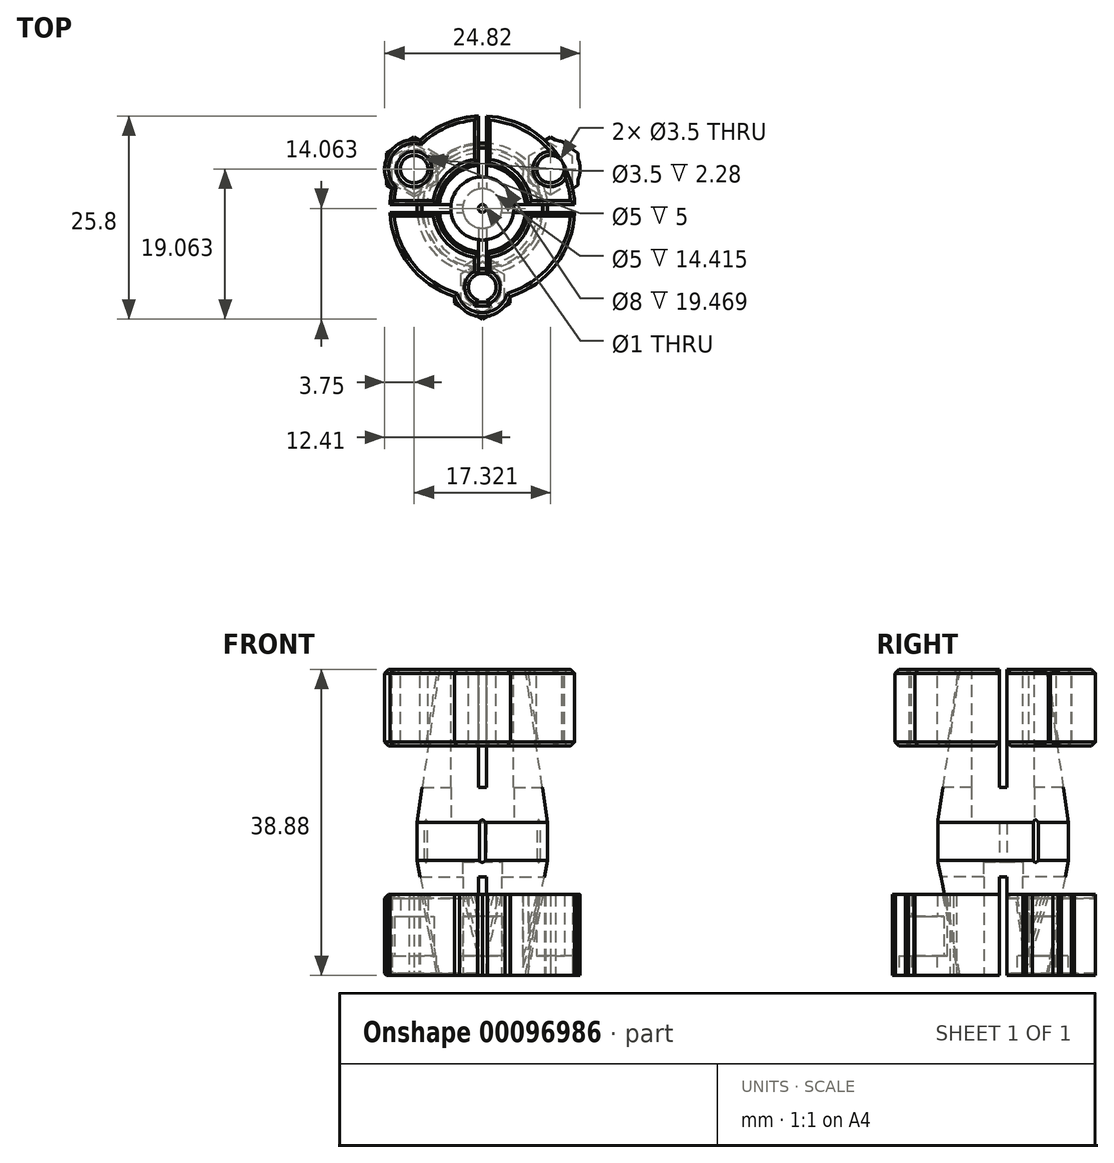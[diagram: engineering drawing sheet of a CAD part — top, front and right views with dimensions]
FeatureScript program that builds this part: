
annotation { "Feature Type Name" : "Feature", "Feature Type Description" : "" }
export const myFeature = defineFeature(function(context is Context, id is Id, definition is map)
    precondition{}
    {
        {
            var Q0;
            Q0=qCreatedBy(makeId("Right.planeOp"),FACE);
            var sketch = newSketch(context, id + "F0", { "sketchPlane" : qUnion([Q0])});
            skLineSegment(sketch, "E0", {"start": v(7.15, -27.2) * mm, "end": v(7.15, -12.78) * mm});
            skLineSegment(sketch, "E1", {"start": v(7.15, -12.78) * mm, "end": v(5.15, -12.78) * mm});
            skLineSegment(sketch, "E2", {"start": v(5.15, -12.78) * mm, "end": v(5.15, -7.78) * mm});
            skLineSegment(sketch, "E3", {"start": v(5.15, -7.78) * mm, "end": v(8.65, -7.78) * mm});
            skLineSegment(sketch, "E4", {"start": v(8.65, -7.78) * mm, "end": v(8.65, 11.68) * mm});
            skLineSegment(sketch, "E5", {"start": v(8.65, 11.68) * mm, "end": v(10.13, 11.68) * mm});
            skLineSegment(sketch, "E6", {"start": v(10.13, 11.68) * mm, "end": v(12.95, -7.78) * mm});
            skLineSegment(sketch, "E7", {"start": v(12.95, -7.78) * mm, "end": v(12.95, -12.57) * mm});
            skLineSegment(sketch, "E8", {"start": v(12.95, -12.57) * mm, "end": v(10.13, -27.2) * mm});
            skLineSegment(sketch, "E9", {"start": v(10.13, -27.2) * mm, "end": v(7.15, -27.2) * mm});
            skLineSegment(sketch, "E10", {"start": v(4.65, -27.22) * mm, "end": v(4.65, -0.97) * mm});
            skLineSegment(sketch, "E11", {"start": v(11.8, 1.95) * mm, "end": v(10.39, 11.68) * mm});
            skPoint(sketch, "E11.startSnap0", {"position": v(11.54, 1.95) * mm});
            skLineSegment(sketch, "E12", {"start": v(10.39, 11.68) * mm, "end": v(16.4, 11.68) * mm});
            skLineSegment(sketch, "E13", {"start": v(16.4, 11.68) * mm, "end": v(16.4, 1.95) * mm});
            skLineSegment(sketch, "E14", {"start": v(16.4, 1.95) * mm, "end": v(11.8, 1.95) * mm});
            skLineSegment(sketch, "E15", {"start": v(10.39, -27.2) * mm, "end": v(12.37, -16.92) * mm});
            skLineSegment(sketch, "E16", {"start": v(12.37, -16.92) * mm, "end": v(16.4, -16.92) * mm});
            skLineSegment(sketch, "E17", {"start": v(16.4, -16.92) * mm, "end": v(16.4, -27.2) * mm});
            skLineSegment(sketch, "E18", {"start": v(16.4, -27.2) * mm, "end": v(10.39, -27.2) * mm});
            skSolve(sketch);
        }
        {
            var Q0;
            Q0=makeQuery(id+"F0.imprint","IMPRINT",FACE,{"disambiguationData":[TD([[makeQuery(id+"F0.imprint","IMPRINT",EDGE,{"derivedFrom":sQuery(id+"F0.wireOp",EDGE,"E0")}),-1.0]])]});
            var Q1;
            Q1=sQuery(id+"F0.wireOp",EDGE,"E10");
            revolve(context, id + "F1", {"entities" : qUnion([Q0]), "axis" : qUnion([Q1]), "revolveType" : RevolveType.FULL});
        }
        {
            var Q0;
            Q0=makeQuery(id+"F0.imprint","IMPRINT",FACE,{"disambiguationData":[TD([[makeQuery(id+"F0.imprint","IMPRINT",EDGE,{"derivedFrom":sQuery(id+"F0.wireOp",EDGE,"E11")}),-1.0]])]});
            var Q1;
            Q1=makeQuery(id+"F0.imprint","IMPRINT",FACE,{"disambiguationData":[TD([[makeQuery(id+"F0.imprint","IMPRINT",EDGE,{"derivedFrom":sQuery(id+"F0.wireOp",EDGE,"E15")}),-1.0]])]});
            var Q2;
            Q2=sQuery(id+"F0.wireOp",EDGE,"E10");
            revolve(context, id + "F2", {"entities" : qUnion([Q0, Q1]), "axis" : qUnion([Q2]), "revolveType" : RevolveType.FULL});
        }
        {
            var Q0;
            Q0=makeQuery(id+"F2.opRevolve","SWEPT_FACE",FACE,{"disambiguationData":[OSD([sQuery(id+"F0.wireOp",EDGE,"E12")])]});
            var sketch = newSketch(context, id + "F3", { "sketchPlane" : qUnion([Q0])});
            skCircle(sketch, "E19", {"center": v(0, 4.65) * mm, "radius": 10 * mm});
            skCircle(sketch, "E20", {"center": v(0, -5.35) * mm, "radius": 1.75 * mm});
            skCircle(sketch, "E21", {"center": v(0, -5.35) * mm, "radius": 3.75 * mm});
            skCircle(sketch, "E22.1.0", {"center": v(8.66, 9.65) * mm, "radius": 1.75 * mm});
            skCircle(sketch, "E22.1.1", {"center": v(8.66, 9.65) * mm, "radius": 3.75 * mm});
            skCircle(sketch, "E22.2.0", {"center": v(-8.66, 9.65) * mm, "radius": 1.75 * mm});
            skCircle(sketch, "E22.2.1", {"center": v(-8.66, 9.65) * mm, "radius": 3.75 * mm});
            skSolve(sketch);
        }
        {
            var Q0;
            {var subQ0=sQuery(id+"F3.wireOp",EDGE,"E20");var subQ1=makeQuery(id+"F2.opRevolve","SWEPT_EDGE",EDGE,{"disambiguationData":[OSD([sQuery(id+"F0.wireOp",EDGE,"E12"),sQuery(id+"F0.wireOp",EDGE,"E13")])]});var subQ2=makeQuery(id+"F3.imprint","INTERSECT",VERTEX,{"disambiguationData":[OD(0.0)],"derivedFrom":[subQ1,subQ0]});Q0=makeQuery(id+"F3.imprint","IMPRINT",FACE,{"disambiguationData":[TD([[makeQuery(id+"F3.imprint","IMPRINT",EDGE,{"disambiguationData":[TD([[subQ2,-1.0]])],"derivedFrom":subQ0}),-1.0]])]});}
            var Q1;
            {var subQ0=sQuery(id+"F3.wireOp",EDGE,"E22.2.0");var subQ1=makeQuery(id+"F2.opRevolve","SWEPT_EDGE",EDGE,{"disambiguationData":[OSD([sQuery(id+"F0.wireOp",EDGE,"E12"),sQuery(id+"F0.wireOp",EDGE,"E13")])]});var subQ2=makeQuery(id+"F3.imprint","INTERSECT",VERTEX,{"disambiguationData":[OD(0.0)],"derivedFrom":[subQ1,subQ0]});Q1=makeQuery(id+"F3.imprint","IMPRINT",FACE,{"disambiguationData":[TD([[makeQuery(id+"F3.imprint","IMPRINT",EDGE,{"disambiguationData":[TD([[subQ2,-1.0]])],"derivedFrom":subQ0}),-1.0]])]});}
            var Q2;
            {var subQ0=sQuery(id+"F3.wireOp",EDGE,"E22.1.0");var subQ1=makeQuery(id+"F2.opRevolve","SWEPT_EDGE",EDGE,{"disambiguationData":[OSD([sQuery(id+"F0.wireOp",EDGE,"E12"),sQuery(id+"F0.wireOp",EDGE,"E13")])]});var subQ2=makeQuery(id+"F3.imprint","INTERSECT",VERTEX,{"disambiguationData":[OD(0.0)],"derivedFrom":[subQ1,subQ0]});Q2=makeQuery(id+"F3.imprint","IMPRINT",FACE,{"disambiguationData":[TD([[makeQuery(id+"F3.imprint","IMPRINT",EDGE,{"disambiguationData":[TD([[subQ2,-1.0]])],"derivedFrom":subQ0}),-1.0]])]});}
            var Q3;
            Q3=makeQuery(id+"F2.opRevolve","SWEPT_FACE",FACE,{"disambiguationData":[OSD([sQuery(id+"F0.wireOp",EDGE,"E14")])]});
            extrude(context, id + "F4", {"entities" : qUnion([Q0, Q1, Q2]), "operationType" : NewBodyOperationType.ADD, "endBound" : BoundingType.UP_TO_SURFACE, "oppositeDirection" : true, "endBoundEntityFace" : qUnion([Q3]), "depth" : 25 * mm});
        }
        {
            var Q0;
            {var subQ0=sQuery(id+"F3.wireOp",EDGE,"E20");var subQ1=sQuery(id+"F3.wireOp",EDGE,"E19");var subQ2=makeQuery(id+"F3.imprint","INTERSECT",VERTEX,{"disambiguationData":[OD(0.0)],"derivedFrom":[subQ1,subQ0]});Q0=makeQuery(id+"F3.imprint","IMPRINT",FACE,{"disambiguationData":[TD([[makeQuery(id+"F3.imprint","IMPRINT",EDGE,{"disambiguationData":[TD([[subQ2,-1.0]])],"derivedFrom":subQ1}),-1.0]])]});}
            var Q1;
            {var subQ0=sQuery(id+"F3.wireOp",EDGE,"E20");var subQ1=sQuery(id+"F3.wireOp",EDGE,"E19");var subQ2=makeQuery(id+"F3.imprint","INTERSECT",VERTEX,{"disambiguationData":[OD(0.0)],"derivedFrom":[subQ1,subQ0]});Q1=makeQuery(id+"F3.imprint","IMPRINT",FACE,{"disambiguationData":[TD([[makeQuery(id+"F3.imprint","IMPRINT",EDGE,{"disambiguationData":[TD([[subQ2,-1.0]])],"derivedFrom":subQ1}),1.0]])]});}
            var Q2;
            {var subQ0=sQuery(id+"F3.wireOp",EDGE,"E22.1.0");var subQ1=sQuery(id+"F3.wireOp",EDGE,"E19");var subQ2=makeQuery(id+"F3.imprint","INTERSECT",VERTEX,{"disambiguationData":[OD(0.0)],"derivedFrom":[subQ1,subQ0]});Q2=makeQuery(id+"F3.imprint","IMPRINT",FACE,{"disambiguationData":[TD([[makeQuery(id+"F3.imprint","IMPRINT",EDGE,{"disambiguationData":[TD([[subQ2,-1.0]])],"derivedFrom":subQ1}),1.0]])]});}
            var Q3;
            {var subQ0=sQuery(id+"F3.wireOp",EDGE,"E22.1.0");var subQ1=sQuery(id+"F3.wireOp",EDGE,"E19");var subQ2=makeQuery(id+"F3.imprint","INTERSECT",VERTEX,{"disambiguationData":[OD(0.0)],"derivedFrom":[subQ1,subQ0]});Q3=makeQuery(id+"F3.imprint","IMPRINT",FACE,{"disambiguationData":[TD([[makeQuery(id+"F3.imprint","IMPRINT",EDGE,{"disambiguationData":[TD([[subQ2,-1.0]])],"derivedFrom":subQ1}),-1.0]])]});}
            var Q4;
            {var subQ0=sQuery(id+"F3.wireOp",EDGE,"E22.2.0");var subQ1=sQuery(id+"F3.wireOp",EDGE,"E19");var subQ2=makeQuery(id+"F3.imprint","INTERSECT",VERTEX,{"disambiguationData":[OD(0.0)],"derivedFrom":[subQ1,subQ0]});Q4=makeQuery(id+"F3.imprint","IMPRINT",FACE,{"disambiguationData":[TD([[makeQuery(id+"F3.imprint","IMPRINT",EDGE,{"disambiguationData":[TD([[subQ2,-1.0]])],"derivedFrom":subQ1}),1.0]])]});}
            var Q5;
            {var subQ0=sQuery(id+"F3.wireOp",EDGE,"E22.2.0");var subQ1=sQuery(id+"F3.wireOp",EDGE,"E19");var subQ2=makeQuery(id+"F3.imprint","INTERSECT",VERTEX,{"disambiguationData":[OD(0.0)],"derivedFrom":[subQ1,subQ0]});Q5=makeQuery(id+"F3.imprint","IMPRINT",FACE,{"disambiguationData":[TD([[makeQuery(id+"F3.imprint","IMPRINT",EDGE,{"disambiguationData":[TD([[subQ2,-1.0]])],"derivedFrom":subQ1}),-1.0]])]});}
            extrude(context, id + "F5", {"entities" : qUnion([Q0, Q1, Q2, Q3, Q4, Q5]), "operationType" : NewBodyOperationType.REMOVE, "oppositeDirection" : true, "depth" : 25 * mm});
        }
        {
            var Q0;
            Q0=makeQuery(id+"F2.opRevolve","SWEPT_FACE",FACE,{"disambiguationData":[OSD([sQuery(id+"F0.wireOp",EDGE,"E18")])]});
            var sketch = newSketch(context, id + "F6", { "sketchPlane" : qUnion([Q0])});
            skArc(sketch, "E23.0.0", {"start": v(-3.55, 6.54) * mm, "mid": v(-10.17, 1.22) * mm, "end": v(-11.47, -7.17) * mm});
            skArc(sketch, "E23.0.1", {"start": v(-11.47, -7.17) * mm, "mid": v(-11.9, -11.53) * mm, "end": v(-7.92, -13.33) * mm});
            skArc(sketch, "E23.0.2", {"start": v(-7.92, -13.33) * mm, "mid": v(0, -16.4) * mm, "end": v(7.92, -13.33) * mm});
            skArc(sketch, "E23.0.3", {"start": v(7.92, -13.33) * mm, "mid": v(11.9, -11.53) * mm, "end": v(11.47, -7.17) * mm});
            skArc(sketch, "E23.0.4", {"start": v(11.47, -7.17) * mm, "mid": v(10.17, 1.22) * mm, "end": v(3.55, 6.54) * mm});
            skArc(sketch, "E23.0.5", {"start": v(3.55, 6.54) * mm, "mid": v(0, 9.1) * mm, "end": v(-3.55, 6.54) * mm});
            skCircle(sketch, "E24", {"center": v(8.66, -9.65) * mm, "radius": 1.75 * mm});
            skCircle(sketch, "E25", {"center": v(-8.66, -9.65) * mm, "radius": 1.75 * mm});
            skCircle(sketch, "E26", {"center": v(0, 5.35) * mm, "radius": 1.75 * mm});
            skSolve(sketch);
        }
        {
            var Q0;
            {var subQ0=sQuery(id+"F6.wireOp",EDGE,"E23.0.5");Q0=makeQuery(id+"F6.imprint","IMPRINT",FACE,{"disambiguationData":[TD([[makeQuery(id+"F6.imprint","IMPRINT",EDGE,{"derivedFrom":subQ0}),1.0]])]});}
            var Q1;
            {var subQ0=sQuery(id+"F6.wireOp",EDGE,"E23.0.3");Q1=makeQuery(id+"F6.imprint","IMPRINT",FACE,{"disambiguationData":[TD([[makeQuery(id+"F6.imprint","IMPRINT",EDGE,{"derivedFrom":subQ0}),1.0]])]});}
            var Q2;
            {var subQ0=sQuery(id+"F6.wireOp",EDGE,"E23.0.1");Q2=makeQuery(id+"F6.imprint","IMPRINT",FACE,{"disambiguationData":[TD([[makeQuery(id+"F6.imprint","IMPRINT",EDGE,{"derivedFrom":subQ0}),1.0]])]});}
            var Q3;
            Q3=makeQuery(id+"F2.opRevolve","SWEPT_FACE",FACE,{"disambiguationData":[OSD([sQuery(id+"F0.wireOp",EDGE,"E16")])]});
            extrude(context, id + "F7", {"entities" : qUnion([Q0, Q1, Q2]), "operationType" : NewBodyOperationType.ADD, "endBound" : BoundingType.UP_TO_SURFACE, "oppositeDirection" : true, "endBoundEntityFace" : qUnion([Q3]), "depth" : 25 * mm});
        }
        {
            var Q0;
            {var subQ0=sQuery(id+"F6.wireOp",EDGE,"E26");var subQ1=makeQuery(id+"F2.opRevolve","SWEPT_EDGE",EDGE,{"disambiguationData":[OSD([sQuery(id+"F0.wireOp",EDGE,"E17"),sQuery(id+"F0.wireOp",EDGE,"E18")])]});var subQ2=makeQuery(id+"F6.imprint","INTERSECT",VERTEX,{"disambiguationData":[OD(0.0)],"derivedFrom":[subQ1,subQ0]});Q0=makeQuery(id+"F6.imprint","IMPRINT",FACE,{"disambiguationData":[TD([[makeQuery(id+"F6.imprint","IMPRINT",EDGE,{"disambiguationData":[TD([[subQ2,-1.0]])],"derivedFrom":subQ0}),1.0]])]});}
            var Q1;
            {var subQ0=sQuery(id+"F6.wireOp",EDGE,"E25");var subQ1=makeQuery(id+"F2.opRevolve","SWEPT_EDGE",EDGE,{"disambiguationData":[OSD([sQuery(id+"F0.wireOp",EDGE,"E17"),sQuery(id+"F0.wireOp",EDGE,"E18")])]});var subQ2=makeQuery(id+"F6.imprint","INTERSECT",VERTEX,{"disambiguationData":[OD(0.0)],"derivedFrom":[subQ1,subQ0]});Q1=makeQuery(id+"F6.imprint","IMPRINT",FACE,{"disambiguationData":[TD([[makeQuery(id+"F6.imprint","IMPRINT",EDGE,{"disambiguationData":[TD([[subQ2,1.0]])],"derivedFrom":subQ0}),1.0]])]});}
            var Q2;
            {var subQ0=sQuery(id+"F6.wireOp",EDGE,"E24");var subQ1=makeQuery(id+"F2.opRevolve","SWEPT_EDGE",EDGE,{"disambiguationData":[OSD([sQuery(id+"F0.wireOp",EDGE,"E17"),sQuery(id+"F0.wireOp",EDGE,"E18")])]});var subQ2=makeQuery(id+"F6.imprint","INTERSECT",VERTEX,{"disambiguationData":[OD(0.0)],"derivedFrom":[subQ1,subQ0]});Q2=makeQuery(id+"F6.imprint","IMPRINT",FACE,{"disambiguationData":[TD([[makeQuery(id+"F6.imprint","IMPRINT",EDGE,{"disambiguationData":[TD([[subQ2,1.0]])],"derivedFrom":subQ0}),1.0]])]});}
            extrude(context, id + "F8", {"entities" : qUnion([Q0, Q1, Q2]), "operationType" : NewBodyOperationType.REMOVE, "oppositeDirection" : true, "depth" : 25 * mm});
        }
        {
            var Q0;
            Q0=makeQuery(id+"F1.opRevolve","SWEPT_FACE",FACE,{"disambiguationData":[OSD([sQuery(id+"F0.wireOp",EDGE,"E5")])]});
            var sketch = newSketch(context, id + "F9", { "sketchPlane" : qUnion([Q0])});
            skLineSegment(sketch, "E27.bottom", {"start": v(0.5, 16.55) * mm, "end": v(-0.5, 16.55) * mm});
            skLineSegment(sketch, "E27.top", {"start": v(0.5, -7.24) * mm, "end": v(-0.5, -7.24) * mm});
            skLineSegment(sketch, "E27.left", {"start": v(0.5, 16.55) * mm, "end": v(0.5, -7.24) * mm});
            skLineSegment(sketch, "E27.right", {"start": v(-0.5, 16.55) * mm, "end": v(-0.5, -7.24) * mm});
            skLineSegment(sketch, "E28.bottom", {"start": v(-15.2, 5.15) * mm, "end": v(15.2, 5.15) * mm});
            skLineSegment(sketch, "E28.top", {"start": v(-15.2, 4.15) * mm, "end": v(15.2, 4.15) * mm});
            skLineSegment(sketch, "E28.left", {"start": v(-15.2, 5.15) * mm, "end": v(-15.2, 4.15) * mm});
            skLineSegment(sketch, "E28.right", {"start": v(15.2, 5.15) * mm, "end": v(15.2, 4.15) * mm});
            skPoint(sketch, "E28.middle", {"position": v(0, 4.65) * mm});
            skSolve(sketch);
        }
        {
            var Q0;
            {var subQ0=sQuery(id+"F9.wireOp",EDGE,"E28.bottom");var subQ1=sQuery(id+"F9.wireOp",EDGE,"E27.left");var subQ2=makeQuery(id+"F9.imprint","INTERSECT",VERTEX,{"derivedFrom":[subQ1,subQ0]});Q0=makeQuery(id+"F9.imprint","IMPRINT",FACE,{"disambiguationData":[TD([[makeQuery(id+"F9.imprint","IMPRINT",EDGE,{"disambiguationData":[TD([[subQ2,-1.0]])],"derivedFrom":subQ1}),-1.0]])]});}
            var Q1;
            {var subQ0=sQuery(id+"F9.wireOp",EDGE,"E27.bottom");Q1=makeQuery(id+"F9.imprint","IMPRINT",FACE,{"disambiguationData":[TD([[makeQuery(id+"F9.imprint","IMPRINT",EDGE,{"derivedFrom":subQ0}),1.0]])]});}
            var Q2;
            {var subQ0=sQuery(id+"F9.wireOp",EDGE,"E27.top");Q2=makeQuery(id+"F9.imprint","IMPRINT",FACE,{"disambiguationData":[TD([[makeQuery(id+"F9.imprint","IMPRINT",EDGE,{"derivedFrom":subQ0}),-1.0]])]});}
            var Q3;
            {var subQ0=sQuery(id+"F9.wireOp",EDGE,"E28.bottom");var subQ1=sQuery(id+"F9.wireOp",EDGE,"E27.left");var subQ2=makeQuery(id+"F9.imprint","INTERSECT",VERTEX,{"derivedFrom":[subQ1,subQ0]});Q3=makeQuery(id+"F9.imprint","IMPRINT",FACE,{"disambiguationData":[TD([[makeQuery(id+"F9.imprint","IMPRINT",EDGE,{"disambiguationData":[TD([[subQ2,1.0]])],"derivedFrom":subQ0}),1.0]])]});}
            var Q4;
            {var subQ0=sQuery(id+"F9.wireOp",EDGE,"E28.top");var subQ1=sQuery(id+"F9.wireOp",EDGE,"E27.left");var subQ2=makeQuery(id+"F9.imprint","INTERSECT",VERTEX,{"derivedFrom":[subQ1,subQ0]});Q4=makeQuery(id+"F9.imprint","IMPRINT",FACE,{"disambiguationData":[TD([[makeQuery(id+"F9.imprint","IMPRINT",EDGE,{"disambiguationData":[TD([[subQ2,1.0]])],"derivedFrom":subQ0}),-1.0]])]});}
            var Q5;
            {var subQ0=sQuery(id+"F9.wireOp",EDGE,"E27.left");var subQ1=sQuery(id+"F0.wireOp",EDGE,"E5");var subQ2=makeQuery(id+"F1.opRevolve","SWEPT_EDGE",EDGE,{"disambiguationData":[OSD([subQ1,sQuery(id+"F0.wireOp",EDGE,"E6")])]});var subQ3=makeQuery(id+"F9.imprint","INTERSECT",VERTEX,{"disambiguationData":[OD(0.0)],"derivedFrom":[subQ2,subQ0]});Q5=makeQuery(id+"F9.imprint","IMPRINT",FACE,{"disambiguationData":[TD([[makeQuery(id+"F9.imprint","IMPRINT",EDGE,{"disambiguationData":[TD([[subQ3,-1.0]])],"derivedFrom":subQ0}),-1.0]])]});}
            var Q6;
            {var subQ0=sQuery(id+"F9.wireOp",EDGE,"E28.bottom");var subQ1=sQuery(id+"F9.wireOp",EDGE,"E27.left");var subQ2=makeQuery(id+"F9.imprint","INTERSECT",VERTEX,{"derivedFrom":[subQ1,subQ0]});Q6=makeQuery(id+"F9.imprint","IMPRINT",FACE,{"disambiguationData":[TD([[makeQuery(id+"F9.imprint","IMPRINT",EDGE,{"disambiguationData":[TD([[subQ2,-1.0]])],"derivedFrom":subQ1}),-1.0]])]});}
            var Q7;
            {var subQ0=sQuery(id+"F9.wireOp",EDGE,"E27.bottom");Q7=makeQuery(id+"F9.imprint","IMPRINT",FACE,{"disambiguationData":[TD([[makeQuery(id+"F9.imprint","IMPRINT",EDGE,{"derivedFrom":subQ0}),1.0]])]});}
            var Q8;
            {var subQ0=sQuery(id+"F9.wireOp",EDGE,"E27.top");Q8=makeQuery(id+"F9.imprint","IMPRINT",FACE,{"disambiguationData":[TD([[makeQuery(id+"F9.imprint","IMPRINT",EDGE,{"derivedFrom":subQ0}),-1.0]])]});}
            var Q9;
            {var subQ0=sQuery(id+"F9.wireOp",EDGE,"E28.bottom");var subQ1=sQuery(id+"F9.wireOp",EDGE,"E27.left");var subQ2=makeQuery(id+"F9.imprint","INTERSECT",VERTEX,{"derivedFrom":[subQ1,subQ0]});Q9=makeQuery(id+"F9.imprint","IMPRINT",FACE,{"disambiguationData":[TD([[makeQuery(id+"F9.imprint","IMPRINT",EDGE,{"disambiguationData":[TD([[subQ2,1.0]])],"derivedFrom":subQ0}),1.0]])]});}
            var Q10;
            {var subQ0=sQuery(id+"F9.wireOp",EDGE,"E28.top");var subQ1=sQuery(id+"F9.wireOp",EDGE,"E27.left");var subQ2=makeQuery(id+"F9.imprint","INTERSECT",VERTEX,{"derivedFrom":[subQ1,subQ0]});Q10=makeQuery(id+"F9.imprint","IMPRINT",FACE,{"disambiguationData":[TD([[makeQuery(id+"F9.imprint","IMPRINT",EDGE,{"disambiguationData":[TD([[subQ2,1.0]])],"derivedFrom":subQ0}),-1.0]])]});}
            var Q11;
            {var subQ0=sQuery(id+"F9.wireOp",EDGE,"E27.left");var subQ1=sQuery(id+"F0.wireOp",EDGE,"E5");var subQ2=makeQuery(id+"F1.opRevolve","SWEPT_EDGE",EDGE,{"disambiguationData":[OSD([subQ1,sQuery(id+"F0.wireOp",EDGE,"E6")])]});var subQ3=makeQuery(id+"F9.imprint","INTERSECT",VERTEX,{"disambiguationData":[OD(0.0)],"derivedFrom":[subQ2,subQ0]});Q11=makeQuery(id+"F9.imprint","IMPRINT",FACE,{"disambiguationData":[TD([[makeQuery(id+"F9.imprint","IMPRINT",EDGE,{"disambiguationData":[TD([[subQ3,-1.0]])],"derivedFrom":subQ0}),-1.0]])]});}
            var Q12;
            {var subQ0=sQuery(id+"F9.wireOp",EDGE,"E28.bottom");var subQ1=sQuery(id+"F9.wireOp",EDGE,"E27.left");var subQ2=makeQuery(id+"F9.imprint","INTERSECT",VERTEX,{"derivedFrom":[subQ1,subQ0]});Q12=makeQuery(id+"F9.imprint","IMPRINT",FACE,{"disambiguationData":[TD([[makeQuery(id+"F9.imprint","IMPRINT",EDGE,{"disambiguationData":[TD([[subQ2,-1.0]])],"derivedFrom":subQ1}),-1.0]])]});}
            var Q13;
            {var subQ0=sQuery(id+"F9.wireOp",EDGE,"E27.bottom");Q13=makeQuery(id+"F9.imprint","IMPRINT",FACE,{"disambiguationData":[TD([[makeQuery(id+"F9.imprint","IMPRINT",EDGE,{"derivedFrom":subQ0}),1.0]])]});}
            var Q14;
            {var subQ0=sQuery(id+"F9.wireOp",EDGE,"E27.top");Q14=makeQuery(id+"F9.imprint","IMPRINT",FACE,{"disambiguationData":[TD([[makeQuery(id+"F9.imprint","IMPRINT",EDGE,{"derivedFrom":subQ0}),-1.0]])]});}
            var Q15;
            {var subQ0=sQuery(id+"F9.wireOp",EDGE,"E28.bottom");var subQ1=sQuery(id+"F9.wireOp",EDGE,"E27.left");var subQ2=makeQuery(id+"F9.imprint","INTERSECT",VERTEX,{"derivedFrom":[subQ1,subQ0]});Q15=makeQuery(id+"F9.imprint","IMPRINT",FACE,{"disambiguationData":[TD([[makeQuery(id+"F9.imprint","IMPRINT",EDGE,{"disambiguationData":[TD([[subQ2,1.0]])],"derivedFrom":subQ0}),1.0]])]});}
            var Q16;
            {var subQ0=sQuery(id+"F9.wireOp",EDGE,"E28.top");var subQ1=sQuery(id+"F9.wireOp",EDGE,"E27.left");var subQ2=makeQuery(id+"F9.imprint","INTERSECT",VERTEX,{"derivedFrom":[subQ1,subQ0]});Q16=makeQuery(id+"F9.imprint","IMPRINT",FACE,{"disambiguationData":[TD([[makeQuery(id+"F9.imprint","IMPRINT",EDGE,{"disambiguationData":[TD([[subQ2,1.0]])],"derivedFrom":subQ0}),-1.0]])]});}
            var Q17;
            {var subQ0=sQuery(id+"F9.wireOp",EDGE,"E27.left");var subQ1=sQuery(id+"F0.wireOp",EDGE,"E5");var subQ2=makeQuery(id+"F1.opRevolve","SWEPT_EDGE",EDGE,{"disambiguationData":[OSD([subQ1,sQuery(id+"F0.wireOp",EDGE,"E6")])]});var subQ3=makeQuery(id+"F9.imprint","INTERSECT",VERTEX,{"disambiguationData":[OD(0.0)],"derivedFrom":[subQ2,subQ0]});Q17=makeQuery(id+"F9.imprint","IMPRINT",FACE,{"disambiguationData":[TD([[makeQuery(id+"F9.imprint","IMPRINT",EDGE,{"disambiguationData":[TD([[subQ3,-1.0]])],"derivedFrom":subQ0}),-1.0]])]});}
            var Q18;
            {var subQ0=sQuery(id+"F9.wireOp",EDGE,"E28.bottom");var subQ1=sQuery(id+"F9.wireOp",EDGE,"E27.left");var subQ2=makeQuery(id+"F9.imprint","INTERSECT",VERTEX,{"derivedFrom":[subQ1,subQ0]});Q18=makeQuery(id+"F9.imprint","IMPRINT",FACE,{"disambiguationData":[TD([[makeQuery(id+"F9.imprint","IMPRINT",EDGE,{"disambiguationData":[TD([[subQ2,-1.0]])],"derivedFrom":subQ1}),-1.0]])]});}
            var Q19;
            {var subQ0=sQuery(id+"F9.wireOp",EDGE,"E27.bottom");Q19=makeQuery(id+"F9.imprint","IMPRINT",FACE,{"disambiguationData":[TD([[makeQuery(id+"F9.imprint","IMPRINT",EDGE,{"derivedFrom":subQ0}),1.0]])]});}
            var Q20;
            {var subQ0=sQuery(id+"F9.wireOp",EDGE,"E27.top");Q20=makeQuery(id+"F9.imprint","IMPRINT",FACE,{"disambiguationData":[TD([[makeQuery(id+"F9.imprint","IMPRINT",EDGE,{"derivedFrom":subQ0}),-1.0]])]});}
            var Q21;
            {var subQ0=sQuery(id+"F9.wireOp",EDGE,"E28.bottom");var subQ1=sQuery(id+"F9.wireOp",EDGE,"E27.left");var subQ2=makeQuery(id+"F9.imprint","INTERSECT",VERTEX,{"derivedFrom":[subQ1,subQ0]});Q21=makeQuery(id+"F9.imprint","IMPRINT",FACE,{"disambiguationData":[TD([[makeQuery(id+"F9.imprint","IMPRINT",EDGE,{"disambiguationData":[TD([[subQ2,1.0]])],"derivedFrom":subQ0}),1.0]])]});}
            var Q22;
            {var subQ0=sQuery(id+"F9.wireOp",EDGE,"E28.top");var subQ1=sQuery(id+"F9.wireOp",EDGE,"E27.left");var subQ2=makeQuery(id+"F9.imprint","INTERSECT",VERTEX,{"derivedFrom":[subQ1,subQ0]});Q22=makeQuery(id+"F9.imprint","IMPRINT",FACE,{"disambiguationData":[TD([[makeQuery(id+"F9.imprint","IMPRINT",EDGE,{"disambiguationData":[TD([[subQ2,1.0]])],"derivedFrom":subQ0}),-1.0]])]});}
            var Q23;
            {var subQ0=sQuery(id+"F9.wireOp",EDGE,"E27.left");var subQ1=sQuery(id+"F0.wireOp",EDGE,"E5");var subQ2=makeQuery(id+"F1.opRevolve","SWEPT_EDGE",EDGE,{"disambiguationData":[OSD([subQ1,sQuery(id+"F0.wireOp",EDGE,"E6")])]});var subQ3=makeQuery(id+"F9.imprint","INTERSECT",VERTEX,{"disambiguationData":[OD(0.0)],"derivedFrom":[subQ2,subQ0]});Q23=makeQuery(id+"F9.imprint","IMPRINT",FACE,{"disambiguationData":[TD([[makeQuery(id+"F9.imprint","IMPRINT",EDGE,{"disambiguationData":[TD([[subQ3,-1.0]])],"derivedFrom":subQ0}),-1.0]])]});}
            var Q24;
            {var subQ0=sQuery(id+"F9.wireOp",EDGE,"E27.top");Q24=makeQuery(id+"F9.imprint","IMPRINT",FACE,{"disambiguationData":[TD([[makeQuery(id+"F9.imprint","IMPRINT",EDGE,{"derivedFrom":subQ0}),-1.0]])]});}
            var Q25;
            {var subQ0=sQuery(id+"F9.wireOp",EDGE,"E28.top");var subQ1=sQuery(id+"F9.wireOp",EDGE,"E27.left");var subQ2=makeQuery(id+"F9.imprint","INTERSECT",VERTEX,{"derivedFrom":[subQ1,subQ0]});Q25=makeQuery(id+"F9.imprint","IMPRINT",FACE,{"disambiguationData":[TD([[makeQuery(id+"F9.imprint","IMPRINT",EDGE,{"disambiguationData":[TD([[subQ2,-1.0]])],"derivedFrom":subQ1}),1.0]])]});}
            var Q26;
            {var subQ0=sQuery(id+"F9.wireOp",EDGE,"E28.top");var subQ1=sQuery(id+"F9.wireOp",EDGE,"E27.right");var subQ2=makeQuery(id+"F9.imprint","INTERSECT",VERTEX,{"derivedFrom":[subQ1,subQ0]});Q26=makeQuery(id+"F9.imprint","IMPRINT",FACE,{"disambiguationData":[TD([[makeQuery(id+"F9.imprint","IMPRINT",EDGE,{"disambiguationData":[TD([[subQ2,-1.0]])],"derivedFrom":subQ1}),-1.0]])]});}
            var Q27;
            {var subQ0=sQuery(id+"F9.wireOp",EDGE,"E28.top");var subQ1=sQuery(id+"F9.wireOp",EDGE,"E27.left");var subQ2=makeQuery(id+"F9.imprint","INTERSECT",VERTEX,{"derivedFrom":[subQ1,subQ0]});Q27=makeQuery(id+"F9.imprint","IMPRINT",FACE,{"disambiguationData":[TD([[makeQuery(id+"F9.imprint","IMPRINT",EDGE,{"disambiguationData":[TD([[subQ2,-1.0]])],"derivedFrom":subQ1}),1.0]])]});}
            var Q28;
            {var subQ0=sQuery(id+"F9.wireOp",EDGE,"E28.top");var subQ1=sQuery(id+"F9.wireOp",EDGE,"E27.right");var subQ2=makeQuery(id+"F9.imprint","INTERSECT",VERTEX,{"derivedFrom":[subQ1,subQ0]});Q28=makeQuery(id+"F9.imprint","IMPRINT",FACE,{"disambiguationData":[TD([[makeQuery(id+"F9.imprint","IMPRINT",EDGE,{"disambiguationData":[TD([[subQ2,-1.0]])],"derivedFrom":subQ1}),-1.0]])]});}
            var Q29;
            {var subQ0=sQuery(id+"F9.wireOp",EDGE,"E28.bottom");var subQ1=sQuery(id+"F9.wireOp",EDGE,"E27.left");var subQ2=makeQuery(id+"F9.imprint","INTERSECT",VERTEX,{"derivedFrom":[subQ1,subQ0]});Q29=makeQuery(id+"F9.imprint","IMPRINT",FACE,{"disambiguationData":[TD([[makeQuery(id+"F9.imprint","IMPRINT",EDGE,{"disambiguationData":[TD([[subQ2,-1.0]])],"derivedFrom":subQ1}),-1.0]])]});}
            var Q30;
            {var subQ0=sQuery(id+"F9.wireOp",EDGE,"E27.bottom");Q30=makeQuery(id+"F9.imprint","IMPRINT",FACE,{"disambiguationData":[TD([[makeQuery(id+"F9.imprint","IMPRINT",EDGE,{"derivedFrom":subQ0}),1.0]])]});}
            var Q31;
            {var subQ0=sQuery(id+"F9.wireOp",EDGE,"E27.top");Q31=makeQuery(id+"F9.imprint","IMPRINT",FACE,{"disambiguationData":[TD([[makeQuery(id+"F9.imprint","IMPRINT",EDGE,{"derivedFrom":subQ0}),-1.0]])]});}
            var Q32;
            {var subQ0=sQuery(id+"F9.wireOp",EDGE,"E28.bottom");var subQ1=sQuery(id+"F9.wireOp",EDGE,"E27.left");var subQ2=makeQuery(id+"F9.imprint","INTERSECT",VERTEX,{"derivedFrom":[subQ1,subQ0]});Q32=makeQuery(id+"F9.imprint","IMPRINT",FACE,{"disambiguationData":[TD([[makeQuery(id+"F9.imprint","IMPRINT",EDGE,{"disambiguationData":[TD([[subQ2,1.0]])],"derivedFrom":subQ0}),1.0]])]});}
            var Q33;
            {var subQ0=sQuery(id+"F9.wireOp",EDGE,"E28.top");var subQ1=sQuery(id+"F9.wireOp",EDGE,"E27.left");var subQ2=makeQuery(id+"F9.imprint","INTERSECT",VERTEX,{"derivedFrom":[subQ1,subQ0]});Q33=makeQuery(id+"F9.imprint","IMPRINT",FACE,{"disambiguationData":[TD([[makeQuery(id+"F9.imprint","IMPRINT",EDGE,{"disambiguationData":[TD([[subQ2,1.0]])],"derivedFrom":subQ0}),-1.0]])]});}
            var Q34;
            {var subQ0=sQuery(id+"F9.wireOp",EDGE,"E27.left");var subQ1=sQuery(id+"F0.wireOp",EDGE,"E5");var subQ2=makeQuery(id+"F1.opRevolve","SWEPT_EDGE",EDGE,{"disambiguationData":[OSD([subQ1,sQuery(id+"F0.wireOp",EDGE,"E6")])]});var subQ3=makeQuery(id+"F9.imprint","INTERSECT",VERTEX,{"disambiguationData":[OD(0.0)],"derivedFrom":[subQ2,subQ0]});Q34=makeQuery(id+"F9.imprint","IMPRINT",FACE,{"disambiguationData":[TD([[makeQuery(id+"F9.imprint","IMPRINT",EDGE,{"disambiguationData":[TD([[subQ3,-1.0]])],"derivedFrom":subQ0}),-1.0]])]});}
            var Q35;
            {var subQ0=sQuery(id+"F9.wireOp",EDGE,"E27.left");var subQ1=sQuery(id+"F0.wireOp",EDGE,"E5");var subQ2=makeQuery(id+"F1.opRevolve","SWEPT_EDGE",EDGE,{"disambiguationData":[OSD([subQ1,sQuery(id+"F0.wireOp",EDGE,"E6")])]});var subQ3=makeQuery(id+"F9.imprint","INTERSECT",VERTEX,{"disambiguationData":[OD(1.0)],"derivedFrom":[subQ2,subQ0]});Q35=makeQuery(id+"F9.imprint","IMPRINT",FACE,{"disambiguationData":[TD([[makeQuery(id+"F9.imprint","IMPRINT",EDGE,{"disambiguationData":[TD([[subQ3,1.0]])],"derivedFrom":subQ0}),-1.0]])]});}
            var Q36;
            {var subQ0=sQuery(id+"F9.wireOp",EDGE,"E28.bottom");var subQ1=sQuery(id+"F9.wireOp",EDGE,"E27.left");var subQ2=makeQuery(id+"F9.imprint","INTERSECT",VERTEX,{"derivedFrom":[subQ1,subQ0]});Q36=makeQuery(id+"F9.imprint","IMPRINT",FACE,{"disambiguationData":[TD([[makeQuery(id+"F9.imprint","IMPRINT",EDGE,{"disambiguationData":[TD([[subQ2,-1.0]])],"derivedFrom":subQ1}),-1.0]])]});}
            var Q37;
            {var subQ0=sQuery(id+"F9.wireOp",EDGE,"E27.bottom");Q37=makeQuery(id+"F9.imprint","IMPRINT",FACE,{"disambiguationData":[TD([[makeQuery(id+"F9.imprint","IMPRINT",EDGE,{"derivedFrom":subQ0}),1.0]])]});}
            var Q38;
            {var subQ0=sQuery(id+"F9.wireOp",EDGE,"E27.top");Q38=makeQuery(id+"F9.imprint","IMPRINT",FACE,{"disambiguationData":[TD([[makeQuery(id+"F9.imprint","IMPRINT",EDGE,{"derivedFrom":subQ0}),-1.0]])]});}
            var Q39;
            {var subQ0=sQuery(id+"F9.wireOp",EDGE,"E28.bottom");var subQ1=sQuery(id+"F9.wireOp",EDGE,"E27.left");var subQ2=makeQuery(id+"F9.imprint","INTERSECT",VERTEX,{"derivedFrom":[subQ1,subQ0]});Q39=makeQuery(id+"F9.imprint","IMPRINT",FACE,{"disambiguationData":[TD([[makeQuery(id+"F9.imprint","IMPRINT",EDGE,{"disambiguationData":[TD([[subQ2,1.0]])],"derivedFrom":subQ0}),1.0]])]});}
            var Q40;
            {var subQ0=sQuery(id+"F9.wireOp",EDGE,"E28.top");var subQ1=sQuery(id+"F9.wireOp",EDGE,"E27.left");var subQ2=makeQuery(id+"F9.imprint","INTERSECT",VERTEX,{"derivedFrom":[subQ1,subQ0]});Q40=makeQuery(id+"F9.imprint","IMPRINT",FACE,{"disambiguationData":[TD([[makeQuery(id+"F9.imprint","IMPRINT",EDGE,{"disambiguationData":[TD([[subQ2,1.0]])],"derivedFrom":subQ0}),-1.0]])]});}
            var Q41;
            {var subQ0=sQuery(id+"F9.wireOp",EDGE,"E27.left");var subQ1=sQuery(id+"F0.wireOp",EDGE,"E5");var subQ2=makeQuery(id+"F1.opRevolve","SWEPT_EDGE",EDGE,{"disambiguationData":[OSD([subQ1,sQuery(id+"F0.wireOp",EDGE,"E6")])]});var subQ3=makeQuery(id+"F9.imprint","INTERSECT",VERTEX,{"disambiguationData":[OD(0.0)],"derivedFrom":[subQ2,subQ0]});Q41=makeQuery(id+"F9.imprint","IMPRINT",FACE,{"disambiguationData":[TD([[makeQuery(id+"F9.imprint","IMPRINT",EDGE,{"disambiguationData":[TD([[subQ3,-1.0]])],"derivedFrom":subQ0}),-1.0]])]});}
            var Q42;
            {var subQ0=sQuery(id+"F9.wireOp",EDGE,"E27.left");var subQ1=sQuery(id+"F0.wireOp",EDGE,"E5");var subQ2=makeQuery(id+"F1.opRevolve","SWEPT_EDGE",EDGE,{"disambiguationData":[OSD([subQ1,sQuery(id+"F0.wireOp",EDGE,"E6")])]});var subQ3=makeQuery(id+"F9.imprint","INTERSECT",VERTEX,{"disambiguationData":[OD(1.0)],"derivedFrom":[subQ2,subQ0]});Q42=makeQuery(id+"F9.imprint","IMPRINT",FACE,{"disambiguationData":[TD([[makeQuery(id+"F9.imprint","IMPRINT",EDGE,{"disambiguationData":[TD([[subQ3,1.0]])],"derivedFrom":subQ0}),-1.0]])]});}
            var Q43;
            {var subQ0=sQuery(id+"F9.wireOp",EDGE,"E28.bottom");var subQ1=sQuery(id+"F9.wireOp",EDGE,"E27.left");var subQ2=makeQuery(id+"F9.imprint","INTERSECT",VERTEX,{"derivedFrom":[subQ1,subQ0]});Q43=makeQuery(id+"F9.imprint","IMPRINT",FACE,{"disambiguationData":[TD([[makeQuery(id+"F9.imprint","IMPRINT",EDGE,{"disambiguationData":[TD([[subQ2,-1.0]])],"derivedFrom":subQ1}),-1.0]])]});}
            var Q44;
            {var subQ0=sQuery(id+"F9.wireOp",EDGE,"E27.bottom");Q44=makeQuery(id+"F9.imprint","IMPRINT",FACE,{"disambiguationData":[TD([[makeQuery(id+"F9.imprint","IMPRINT",EDGE,{"derivedFrom":subQ0}),1.0]])]});}
            var Q45;
            {var subQ0=sQuery(id+"F9.wireOp",EDGE,"E27.top");Q45=makeQuery(id+"F9.imprint","IMPRINT",FACE,{"disambiguationData":[TD([[makeQuery(id+"F9.imprint","IMPRINT",EDGE,{"derivedFrom":subQ0}),-1.0]])]});}
            var Q46;
            {var subQ0=sQuery(id+"F9.wireOp",EDGE,"E28.bottom");var subQ1=sQuery(id+"F9.wireOp",EDGE,"E27.left");var subQ2=makeQuery(id+"F9.imprint","INTERSECT",VERTEX,{"derivedFrom":[subQ1,subQ0]});Q46=makeQuery(id+"F9.imprint","IMPRINT",FACE,{"disambiguationData":[TD([[makeQuery(id+"F9.imprint","IMPRINT",EDGE,{"disambiguationData":[TD([[subQ2,1.0]])],"derivedFrom":subQ0}),1.0]])]});}
            var Q47;
            {var subQ0=sQuery(id+"F9.wireOp",EDGE,"E28.top");var subQ1=sQuery(id+"F9.wireOp",EDGE,"E27.left");var subQ2=makeQuery(id+"F9.imprint","INTERSECT",VERTEX,{"derivedFrom":[subQ1,subQ0]});Q47=makeQuery(id+"F9.imprint","IMPRINT",FACE,{"disambiguationData":[TD([[makeQuery(id+"F9.imprint","IMPRINT",EDGE,{"disambiguationData":[TD([[subQ2,1.0]])],"derivedFrom":subQ0}),-1.0]])]});}
            var Q48;
            {var subQ0=sQuery(id+"F9.wireOp",EDGE,"E27.left");var subQ1=sQuery(id+"F0.wireOp",EDGE,"E5");var subQ2=makeQuery(id+"F1.opRevolve","SWEPT_EDGE",EDGE,{"disambiguationData":[OSD([subQ1,sQuery(id+"F0.wireOp",EDGE,"E6")])]});var subQ3=makeQuery(id+"F9.imprint","INTERSECT",VERTEX,{"disambiguationData":[OD(0.0)],"derivedFrom":[subQ2,subQ0]});Q48=makeQuery(id+"F9.imprint","IMPRINT",FACE,{"disambiguationData":[TD([[makeQuery(id+"F9.imprint","IMPRINT",EDGE,{"disambiguationData":[TD([[subQ3,-1.0]])],"derivedFrom":subQ0}),-1.0]])]});}
            var Q49;
            {var subQ0=sQuery(id+"F9.wireOp",EDGE,"E27.left");var subQ1=sQuery(id+"F0.wireOp",EDGE,"E5");var subQ2=makeQuery(id+"F1.opRevolve","SWEPT_EDGE",EDGE,{"disambiguationData":[OSD([subQ1,sQuery(id+"F0.wireOp",EDGE,"E6")])]});var subQ3=makeQuery(id+"F9.imprint","INTERSECT",VERTEX,{"disambiguationData":[OD(1.0)],"derivedFrom":[subQ2,subQ0]});Q49=makeQuery(id+"F9.imprint","IMPRINT",FACE,{"disambiguationData":[TD([[makeQuery(id+"F9.imprint","IMPRINT",EDGE,{"disambiguationData":[TD([[subQ3,1.0]])],"derivedFrom":subQ0}),-1.0]])]});}
            var Q50;
            {var subQ0=sQuery(id+"F9.wireOp",EDGE,"E28.bottom");var subQ1=sQuery(id+"F9.wireOp",EDGE,"E27.left");var subQ2=makeQuery(id+"F9.imprint","INTERSECT",VERTEX,{"derivedFrom":[subQ1,subQ0]});Q50=makeQuery(id+"F9.imprint","IMPRINT",FACE,{"disambiguationData":[TD([[makeQuery(id+"F9.imprint","IMPRINT",EDGE,{"disambiguationData":[TD([[subQ2,1.0]])],"derivedFrom":subQ1}),1.0]])]});}
            var Q51;
            {var subQ0=sQuery(id+"F9.wireOp",EDGE,"E28.bottom");var subQ1=sQuery(id+"F9.wireOp",EDGE,"E27.right");var subQ2=makeQuery(id+"F9.imprint","INTERSECT",VERTEX,{"derivedFrom":[subQ1,subQ0]});Q51=makeQuery(id+"F9.imprint","IMPRINT",FACE,{"disambiguationData":[TD([[makeQuery(id+"F9.imprint","IMPRINT",EDGE,{"disambiguationData":[TD([[subQ2,1.0]])],"derivedFrom":subQ1}),-1.0]])]});}
            var Q52;
            {var subQ0=sQuery(id+"F9.wireOp",EDGE,"E28.bottom");var subQ1=sQuery(id+"F9.wireOp",EDGE,"E27.left");var subQ2=makeQuery(id+"F9.imprint","INTERSECT",VERTEX,{"derivedFrom":[subQ1,subQ0]});Q52=makeQuery(id+"F9.imprint","IMPRINT",FACE,{"disambiguationData":[TD([[makeQuery(id+"F9.imprint","IMPRINT",EDGE,{"disambiguationData":[TD([[subQ2,1.0]])],"derivedFrom":subQ1}),1.0]])]});}
            var Q53;
            {var subQ0=sQuery(id+"F9.wireOp",EDGE,"E28.bottom");var subQ1=sQuery(id+"F9.wireOp",EDGE,"E27.right");var subQ2=makeQuery(id+"F9.imprint","INTERSECT",VERTEX,{"derivedFrom":[subQ1,subQ0]});Q53=makeQuery(id+"F9.imprint","IMPRINT",FACE,{"disambiguationData":[TD([[makeQuery(id+"F9.imprint","IMPRINT",EDGE,{"disambiguationData":[TD([[subQ2,1.0]])],"derivedFrom":subQ1}),-1.0]])]});}
            var Q54;
            {var subQ0=sQuery(id+"F9.wireOp",EDGE,"E27.bottom");Q54=makeQuery(id+"F9.imprint","IMPRINT",FACE,{"disambiguationData":[TD([[makeQuery(id+"F9.imprint","IMPRINT",EDGE,{"derivedFrom":subQ0}),1.0]])]});}
            var Q55;
            {var subQ0=sQuery(id+"F9.wireOp",EDGE,"E28.bottom");var subQ1=sQuery(id+"F9.wireOp",EDGE,"E27.left");var subQ2=makeQuery(id+"F9.imprint","INTERSECT",VERTEX,{"derivedFrom":[subQ1,subQ0]});Q55=makeQuery(id+"F9.imprint","IMPRINT",FACE,{"disambiguationData":[TD([[makeQuery(id+"F9.imprint","IMPRINT",EDGE,{"disambiguationData":[TD([[subQ2,1.0]])],"derivedFrom":subQ1}),1.0]])]});}
            var Q56;
            {var subQ0=sQuery(id+"F9.wireOp",EDGE,"E28.top");var subQ1=sQuery(id+"F9.wireOp",EDGE,"E27.left");var subQ2=makeQuery(id+"F9.imprint","INTERSECT",VERTEX,{"derivedFrom":[subQ1,subQ0]});Q56=makeQuery(id+"F9.imprint","IMPRINT",FACE,{"disambiguationData":[TD([[makeQuery(id+"F9.imprint","IMPRINT",EDGE,{"disambiguationData":[TD([[subQ2,-1.0]])],"derivedFrom":subQ1}),1.0]])]});}
            var Q57;
            {var subQ0=sQuery(id+"F9.wireOp",EDGE,"E28.bottom");var subQ1=sQuery(id+"F9.wireOp",EDGE,"E27.left");var subQ2=makeQuery(id+"F9.imprint","INTERSECT",VERTEX,{"derivedFrom":[subQ1,subQ0]});Q57=makeQuery(id+"F9.imprint","IMPRINT",FACE,{"disambiguationData":[TD([[makeQuery(id+"F9.imprint","IMPRINT",EDGE,{"disambiguationData":[TD([[subQ2,1.0]])],"derivedFrom":subQ1}),1.0]])]});}
            var Q58;
            {var subQ0=sQuery(id+"F9.wireOp",EDGE,"E28.top");var subQ1=sQuery(id+"F9.wireOp",EDGE,"E27.left");var subQ2=makeQuery(id+"F9.imprint","INTERSECT",VERTEX,{"derivedFrom":[subQ1,subQ0]});Q58=makeQuery(id+"F9.imprint","IMPRINT",FACE,{"disambiguationData":[TD([[makeQuery(id+"F9.imprint","IMPRINT",EDGE,{"disambiguationData":[TD([[subQ2,-1.0]])],"derivedFrom":subQ1}),1.0]])]});}
            var Q59;
            {var subQ0=sQuery(id+"F9.wireOp",EDGE,"E28.right");Q59=makeQuery(id+"F9.imprint","IMPRINT",FACE,{"disambiguationData":[TD([[makeQuery(id+"F9.imprint","IMPRINT",EDGE,{"derivedFrom":subQ0}),-1.0]])]});}
            var Q60;
            {var subQ0=sQuery(id+"F9.wireOp",EDGE,"E28.bottom");var subQ1=sQuery(id+"F9.wireOp",EDGE,"E27.right");var subQ2=makeQuery(id+"F9.imprint","INTERSECT",VERTEX,{"derivedFrom":[subQ1,subQ0]});Q60=makeQuery(id+"F9.imprint","IMPRINT",FACE,{"disambiguationData":[TD([[makeQuery(id+"F9.imprint","IMPRINT",EDGE,{"disambiguationData":[TD([[subQ2,1.0]])],"derivedFrom":subQ1}),-1.0]])]});}
            var Q61;
            {var subQ0=sQuery(id+"F9.wireOp",EDGE,"E28.top");var subQ1=sQuery(id+"F9.wireOp",EDGE,"E27.right");var subQ2=makeQuery(id+"F9.imprint","INTERSECT",VERTEX,{"derivedFrom":[subQ1,subQ0]});Q61=makeQuery(id+"F9.imprint","IMPRINT",FACE,{"disambiguationData":[TD([[makeQuery(id+"F9.imprint","IMPRINT",EDGE,{"disambiguationData":[TD([[subQ2,-1.0]])],"derivedFrom":subQ1}),-1.0]])]});}
            var Q62;
            {var subQ0=sQuery(id+"F9.wireOp",EDGE,"E28.bottom");var subQ1=sQuery(id+"F9.wireOp",EDGE,"E27.right");var subQ2=makeQuery(id+"F9.imprint","INTERSECT",VERTEX,{"derivedFrom":[subQ1,subQ0]});Q62=makeQuery(id+"F9.imprint","IMPRINT",FACE,{"disambiguationData":[TD([[makeQuery(id+"F9.imprint","IMPRINT",EDGE,{"disambiguationData":[TD([[subQ2,1.0]])],"derivedFrom":subQ1}),-1.0]])]});}
            var Q63;
            {var subQ0=sQuery(id+"F9.wireOp",EDGE,"E28.top");var subQ1=sQuery(id+"F9.wireOp",EDGE,"E27.right");var subQ2=makeQuery(id+"F9.imprint","INTERSECT",VERTEX,{"derivedFrom":[subQ1,subQ0]});Q63=makeQuery(id+"F9.imprint","IMPRINT",FACE,{"disambiguationData":[TD([[makeQuery(id+"F9.imprint","IMPRINT",EDGE,{"disambiguationData":[TD([[subQ2,-1.0]])],"derivedFrom":subQ1}),-1.0]])]});}
            var Q64;
            {var subQ0=sQuery(id+"F9.wireOp",EDGE,"E28.left");Q64=makeQuery(id+"F9.imprint","IMPRINT",FACE,{"disambiguationData":[TD([[makeQuery(id+"F9.imprint","IMPRINT",EDGE,{"derivedFrom":subQ0}),1.0]])]});}
            var Q65;
            {var subQ0=sQuery(id+"F9.wireOp",EDGE,"E28.bottom");var subQ1=sQuery(id+"F0.wireOp",EDGE,"E5");var subQ2=makeQuery(id+"F1.opRevolve","SWEPT_EDGE",EDGE,{"disambiguationData":[OSD([subQ1,sQuery(id+"F0.wireOp",EDGE,"E6")])]});var subQ3=makeQuery(id+"F9.imprint","INTERSECT",VERTEX,{"disambiguationData":[OD(0.0)],"derivedFrom":[subQ2,subQ0]});Q65=makeQuery(id+"F9.imprint","IMPRINT",FACE,{"disambiguationData":[TD([[makeQuery(id+"F9.imprint","IMPRINT",EDGE,{"disambiguationData":[TD([[subQ3,-1.0]])],"derivedFrom":subQ0}),-1.0]])]});}
            var Q66;
            {var subQ0=sQuery(id+"F9.wireOp",EDGE,"E28.bottom");var subQ1=sQuery(id+"F0.wireOp",EDGE,"E5");var subQ2=makeQuery(id+"F1.opRevolve","SWEPT_EDGE",EDGE,{"disambiguationData":[OSD([subQ1,sQuery(id+"F0.wireOp",EDGE,"E6")])]});var subQ3=makeQuery(id+"F9.imprint","INTERSECT",VERTEX,{"disambiguationData":[OD(1.0)],"derivedFrom":[subQ2,subQ0]});Q66=makeQuery(id+"F9.imprint","IMPRINT",FACE,{"disambiguationData":[TD([[makeQuery(id+"F9.imprint","IMPRINT",EDGE,{"disambiguationData":[TD([[subQ3,1.0]])],"derivedFrom":subQ0}),-1.0]])]});}
            extrude(context, id + "F10", {"entities" : qUnion([Q0, Q1, Q2, Q3, Q4, Q5, Q6, Q7, Q8, Q9, Q10, Q11, Q12, Q13, Q14, Q15, Q16, Q17, Q18, Q19, Q20, Q21, Q22, Q23, Q24, Q25, Q26, Q27, Q28, Q29, Q30, Q31, Q32, Q33, Q34, Q35, Q36, Q37, Q38, Q39, Q40, Q41, Q42, Q43, Q44, Q45, Q46, Q47, Q48, Q49, Q50, Q51, Q52, Q53, Q54, Q55, Q56, Q57, Q58, Q59, Q60, Q61, Q62, Q63, Q64, Q65, Q66]), "operationType" : NewBodyOperationType.REMOVE, "oppositeDirection" : true, "depth" : 15 * mm});
        }
        {
            var Q0;
            {var subQ0=sQuery(id+"F9.wireOp",EDGE,"E28.bottom");var subQ1=sQuery(id+"F9.wireOp",EDGE,"E27.left");var subQ2=makeQuery(id+"F9.imprint","INTERSECT",VERTEX,{"derivedFrom":[subQ1,subQ0]});Q0=makeQuery(id+"F9.imprint","IMPRINT",FACE,{"disambiguationData":[TD([[makeQuery(id+"F9.imprint","IMPRINT",EDGE,{"disambiguationData":[TD([[subQ2,-1.0]])],"derivedFrom":subQ1}),1.0]])]});}
            var Q1;
            {var subQ0=sQuery(id+"F9.wireOp",EDGE,"E28.bottom");var subQ1=sQuery(id+"F0.wireOp",EDGE,"E5");var subQ2=makeQuery(id+"F1.opRevolve","SWEPT_EDGE",EDGE,{"disambiguationData":[OSD([subQ1,sQuery(id+"F0.wireOp",EDGE,"E6")])]});var subQ3=makeQuery(id+"F9.imprint","INTERSECT",VERTEX,{"disambiguationData":[OD(1.0)],"derivedFrom":[subQ2,subQ0]});Q1=makeQuery(id+"F9.imprint","IMPRINT",FACE,{"disambiguationData":[TD([[makeQuery(id+"F9.imprint","IMPRINT",EDGE,{"disambiguationData":[TD([[subQ3,1.0]])],"derivedFrom":subQ0}),-1.0]])]});}
            var Q2;
            {var subQ0=sQuery(id+"F9.wireOp",EDGE,"E28.right");Q2=makeQuery(id+"F9.imprint","IMPRINT",FACE,{"disambiguationData":[TD([[makeQuery(id+"F9.imprint","IMPRINT",EDGE,{"derivedFrom":subQ0}),-1.0]])]});}
            var Q3;
            {var subQ0=sQuery(id+"F9.wireOp",EDGE,"E28.bottom");var subQ1=sQuery(id+"F9.wireOp",EDGE,"E27.left");var subQ2=makeQuery(id+"F9.imprint","INTERSECT",VERTEX,{"derivedFrom":[subQ1,subQ0]});Q3=makeQuery(id+"F9.imprint","IMPRINT",FACE,{"disambiguationData":[TD([[makeQuery(id+"F9.imprint","IMPRINT",EDGE,{"disambiguationData":[TD([[subQ2,1.0]])],"derivedFrom":subQ0}),1.0]])]});}
            var Q4;
            {var subQ0=sQuery(id+"F9.wireOp",EDGE,"E27.left");var subQ1=sQuery(id+"F0.wireOp",EDGE,"E5");var subQ2=makeQuery(id+"F1.opRevolve","SWEPT_EDGE",EDGE,{"disambiguationData":[OSD([subQ1,sQuery(id+"F0.wireOp",EDGE,"E6")])]});var subQ3=makeQuery(id+"F9.imprint","INTERSECT",VERTEX,{"disambiguationData":[OD(0.0)],"derivedFrom":[subQ2,subQ0]});Q4=makeQuery(id+"F9.imprint","IMPRINT",FACE,{"disambiguationData":[TD([[makeQuery(id+"F9.imprint","IMPRINT",EDGE,{"disambiguationData":[TD([[subQ3,-1.0]])],"derivedFrom":subQ0}),-1.0]])]});}
            var Q5;
            {var subQ0=sQuery(id+"F9.wireOp",EDGE,"E27.bottom");Q5=makeQuery(id+"F9.imprint","IMPRINT",FACE,{"disambiguationData":[TD([[makeQuery(id+"F9.imprint","IMPRINT",EDGE,{"derivedFrom":subQ0}),1.0]])]});}
            var Q6;
            {var subQ0=sQuery(id+"F9.wireOp",EDGE,"E27.top");Q6=makeQuery(id+"F9.imprint","IMPRINT",FACE,{"disambiguationData":[TD([[makeQuery(id+"F9.imprint","IMPRINT",EDGE,{"derivedFrom":subQ0}),-1.0]])]});}
            var Q7;
            {var subQ0=sQuery(id+"F9.wireOp",EDGE,"E27.left");var subQ1=sQuery(id+"F0.wireOp",EDGE,"E5");var subQ2=makeQuery(id+"F1.opRevolve","SWEPT_EDGE",EDGE,{"disambiguationData":[OSD([subQ1,sQuery(id+"F0.wireOp",EDGE,"E6")])]});var subQ3=makeQuery(id+"F9.imprint","INTERSECT",VERTEX,{"disambiguationData":[OD(1.0)],"derivedFrom":[subQ2,subQ0]});Q7=makeQuery(id+"F9.imprint","IMPRINT",FACE,{"disambiguationData":[TD([[makeQuery(id+"F9.imprint","IMPRINT",EDGE,{"disambiguationData":[TD([[subQ3,1.0]])],"derivedFrom":subQ0}),-1.0]])]});}
            var Q8;
            {var subQ0=sQuery(id+"F9.wireOp",EDGE,"E28.top");var subQ1=sQuery(id+"F9.wireOp",EDGE,"E27.left");var subQ2=makeQuery(id+"F9.imprint","INTERSECT",VERTEX,{"derivedFrom":[subQ1,subQ0]});Q8=makeQuery(id+"F9.imprint","IMPRINT",FACE,{"disambiguationData":[TD([[makeQuery(id+"F9.imprint","IMPRINT",EDGE,{"disambiguationData":[TD([[subQ2,1.0]])],"derivedFrom":subQ0}),-1.0]])]});}
            var Q9;
            {var subQ0=sQuery(id+"F9.wireOp",EDGE,"E28.left");Q9=makeQuery(id+"F9.imprint","IMPRINT",FACE,{"disambiguationData":[TD([[makeQuery(id+"F9.imprint","IMPRINT",EDGE,{"derivedFrom":subQ0}),1.0]])]});}
            var Q10;
            {var subQ0=sQuery(id+"F9.wireOp",EDGE,"E28.bottom");var subQ1=sQuery(id+"F0.wireOp",EDGE,"E5");var subQ2=makeQuery(id+"F1.opRevolve","SWEPT_EDGE",EDGE,{"disambiguationData":[OSD([subQ1,sQuery(id+"F0.wireOp",EDGE,"E6")])]});var subQ3=makeQuery(id+"F9.imprint","INTERSECT",VERTEX,{"disambiguationData":[OD(0.0)],"derivedFrom":[subQ2,subQ0]});Q10=makeQuery(id+"F9.imprint","IMPRINT",FACE,{"disambiguationData":[TD([[makeQuery(id+"F9.imprint","IMPRINT",EDGE,{"disambiguationData":[TD([[subQ3,-1.0]])],"derivedFrom":subQ0}),-1.0]])]});}
            var Q11;
            {var subQ0=sQuery(id+"F9.wireOp",EDGE,"E28.bottom");var subQ1=sQuery(id+"F9.wireOp",EDGE,"E27.right");var subQ2=makeQuery(id+"F9.imprint","INTERSECT",VERTEX,{"derivedFrom":[subQ1,subQ0]});Q11=makeQuery(id+"F9.imprint","IMPRINT",FACE,{"disambiguationData":[TD([[makeQuery(id+"F9.imprint","IMPRINT",EDGE,{"disambiguationData":[TD([[subQ2,-1.0]])],"derivedFrom":subQ1}),-1.0]])]});}
            extrude(context, id + "F11", {"entities" : qUnion([Q0, Q1, Q2, Q3, Q4, Q5, Q6, Q7, Q8, Q9, Q10, Q11]), "operationType" : NewBodyOperationType.REMOVE, "oppositeDirection" : true, "depth" : 44.88 * mm, "hasSecondDirection" : true, "secondDirectionOppositeDirection" : true, "secondDirectionDepth" : 26.34 * mm});
        }
        {
            var Q0;
            {var subQ0=sQuery(id+"F0.wireOp",EDGE,"E18");var subQ1=sQuery(id+"F0.wireOp",EDGE,"E17");Q0=makeQuery(id+"F7.boolean.opBoolean","MERGE",FACE,{"derivedFrom":[makeQuery(id+"F2.opRevolve","SWEPT_FACE",FACE,{"disambiguationData":[OSD([subQ0])]}),makeQuery(id+"F7.opExtrude","CAP_FACE",FACE,{"disambiguationData":[OSD([subQ1,subQ0,sQuery(id+"F6.wireOp",EDGE,"E23.0.1"),sQuery(id+"F6.wireOp",EDGE,"E25")])],"isStart":true}),makeQuery(id+"F7.opExtrude","CAP_FACE",FACE,{"disambiguationData":[OSD([subQ1,subQ0,sQuery(id+"F6.wireOp",EDGE,"E23.0.3"),sQuery(id+"F6.wireOp",EDGE,"E24")])],"isStart":true}),makeQuery(id+"F7.opExtrude","CAP_FACE",FACE,{"disambiguationData":[OSD([subQ1,subQ0,sQuery(id+"F6.wireOp",EDGE,"E23.0.5"),sQuery(id+"F6.wireOp",EDGE,"E26")])],"isStart":true})]});}
            var sketch = newSketch(context, id + "F12", { "sketchPlane" : qUnion([Q0])});
            skCircle(sketch, "E29.cCircle", {"center": v(8.66, -9.65) * mm, "radius": 2.8 * mm, "construction": true});
            skLineSegment(sketch, "E29.0", {"start": v(5.86, -11.27) * mm, "end": v(5.86, -8.04) * mm});
            skLineSegment(sketch, "E29.1", {"start": v(5.86, -8.04) * mm, "end": v(8.66, -6.42) * mm});
            skLineSegment(sketch, "E29.2", {"start": v(8.66, -6.42) * mm, "end": v(11.46, -8.04) * mm});
            skLineSegment(sketch, "E29.3", {"start": v(11.46, -8.04) * mm, "end": v(11.46, -11.27) * mm});
            skLineSegment(sketch, "E29.4", {"start": v(11.46, -11.27) * mm, "end": v(8.66, -12.89) * mm});
            skLineSegment(sketch, "E29.5", {"start": v(8.66, -12.89) * mm, "end": v(5.86, -11.27) * mm});
            skPoint(sketch, "E29.0.midPoint", {"position": v(5.86, -9.65) * mm});
            skCircle(sketch, "E30.cCircle", {"center": v(8.66, -9.65) * mm, "radius": 3.52 * mm, "construction": true});
            skLineSegment(sketch, "E30.0", {"start": v(5.14, -11.68) * mm, "end": v(5.14, -7.62) * mm});
            skLineSegment(sketch, "E30.1", {"start": v(5.14, -7.62) * mm, "end": v(8.66, -5.6) * mm});
            skLineSegment(sketch, "E30.2", {"start": v(8.66, -5.6) * mm, "end": v(12.18, -7.62) * mm});
            skLineSegment(sketch, "E30.3", {"start": v(12.18, -7.62) * mm, "end": v(12.18, -11.68) * mm});
            skLineSegment(sketch, "E30.4", {"start": v(12.18, -11.68) * mm, "end": v(8.66, -13.71) * mm});
            skLineSegment(sketch, "E30.5", {"start": v(8.66, -13.71) * mm, "end": v(5.14, -11.68) * mm});
            skPoint(sketch, "E30.0.midPoint", {"position": v(5.14, -9.65) * mm});
            skLineSegment(sketch, "E31.1.0", {"start": v(0, 9.4) * mm, "end": v(3.52, 7.38) * mm});
            skLineSegment(sketch, "E31.1.1", {"start": v(3.52, 7.38) * mm, "end": v(3.52, 3.32) * mm});
            skLineSegment(sketch, "E31.1.2", {"start": v(2.8, 6.96) * mm, "end": v(2.8, 3.73) * mm});
            skLineSegment(sketch, "E31.1.3", {"start": v(0, 8.58) * mm, "end": v(2.8, 6.96) * mm});
            skLineSegment(sketch, "E31.1.4", {"start": v(-3.52, 7.38) * mm, "end": v(0, 9.4) * mm});
            skLineSegment(sketch, "E31.1.5", {"start": v(-3.52, 3.32) * mm, "end": v(-3.52, 7.38) * mm});
            skLineSegment(sketch, "E31.1.6", {"start": v(0, 1.29) * mm, "end": v(-3.52, 3.32) * mm});
            skLineSegment(sketch, "E31.1.7", {"start": v(3.52, 3.32) * mm, "end": v(0, 1.29) * mm});
            skLineSegment(sketch, "E31.1.8", {"start": v(2.8, 3.73) * mm, "end": v(0, 2.11) * mm});
            skLineSegment(sketch, "E31.1.9", {"start": v(0, 2.11) * mm, "end": v(-2.8, 3.73) * mm});
            skLineSegment(sketch, "E31.1.10", {"start": v(-2.8, 3.73) * mm, "end": v(-2.8, 6.96) * mm});
            skLineSegment(sketch, "E31.1.11", {"start": v(-2.8, 6.96) * mm, "end": v(0, 8.58) * mm});
            skLineSegment(sketch, "E31.2.0", {"start": v(-12.18, -11.68) * mm, "end": v(-12.18, -7.62) * mm});
            skLineSegment(sketch, "E31.2.1", {"start": v(-12.18, -7.62) * mm, "end": v(-8.66, -5.6) * mm});
            skLineSegment(sketch, "E31.2.2", {"start": v(-11.46, -8.04) * mm, "end": v(-8.66, -6.42) * mm});
            skLineSegment(sketch, "E31.2.3", {"start": v(-11.46, -11.27) * mm, "end": v(-11.46, -8.04) * mm});
            skLineSegment(sketch, "E31.2.4", {"start": v(-8.66, -13.71) * mm, "end": v(-12.18, -11.68) * mm});
            skLineSegment(sketch, "E31.2.5", {"start": v(-5.14, -11.68) * mm, "end": v(-8.66, -13.71) * mm});
            skLineSegment(sketch, "E31.2.6", {"start": v(-5.14, -7.62) * mm, "end": v(-5.14, -11.68) * mm});
            skLineSegment(sketch, "E31.2.7", {"start": v(-8.66, -5.6) * mm, "end": v(-5.14, -7.62) * mm});
            skLineSegment(sketch, "E31.2.8", {"start": v(-8.66, -6.42) * mm, "end": v(-5.86, -8.04) * mm});
            skLineSegment(sketch, "E31.2.9", {"start": v(-5.86, -8.04) * mm, "end": v(-5.86, -11.27) * mm});
            skLineSegment(sketch, "E31.2.10", {"start": v(-5.86, -11.27) * mm, "end": v(-8.66, -12.89) * mm});
            skLineSegment(sketch, "E31.2.11", {"start": v(-8.66, -12.89) * mm, "end": v(-11.46, -11.27) * mm});
            skPoint(sketch, "E31.center", {"position": v(0, -4.65) * mm});
            skSolve(sketch);
        }
        {
            var Q0;
            {var subQ0=sQuery(id+"F12.wireOp",EDGE,"E30.3");var subQ1=sQuery(id+"F12.wireOp",EDGE,"E30.2");var subQ2=makeQuery(id+"F12.imprint","INTERSECT",VERTEX,{"derivedFrom":[subQ1,subQ0]});Q0=makeQuery(id+"F12.imprint","IMPRINT",FACE,{"disambiguationData":[TD([[makeQuery(id+"F12.imprint","IMPRINT",EDGE,{"disambiguationData":[TD([[subQ2,1.0]])],"derivedFrom":subQ1}),-1.0]])]});}
            var Q1;
            {var subQ0=sQuery(id+"F12.wireOp",EDGE,"E30.4");var subQ1=sQuery(id+"F12.wireOp",EDGE,"E30.3");var subQ2=makeQuery(id+"F12.imprint","INTERSECT",VERTEX,{"derivedFrom":[subQ1,subQ0]});Q1=makeQuery(id+"F12.imprint","IMPRINT",FACE,{"disambiguationData":[TD([[makeQuery(id+"F12.imprint","IMPRINT",EDGE,{"disambiguationData":[TD([[subQ2,1.0]])],"derivedFrom":subQ1}),-1.0]])]});}
            var Q2;
            {var subQ0=sQuery(id+"F12.wireOp",EDGE,"E30.5");var subQ1=sQuery(id+"F12.wireOp",EDGE,"E30.4");var subQ2=makeQuery(id+"F12.imprint","INTERSECT",VERTEX,{"derivedFrom":[subQ1,subQ0]});Q2=makeQuery(id+"F12.imprint","IMPRINT",FACE,{"disambiguationData":[TD([[makeQuery(id+"F12.imprint","IMPRINT",EDGE,{"disambiguationData":[TD([[subQ2,1.0]])],"derivedFrom":subQ1}),-1.0]])]});}
            var Q3;
            {var subQ0=sQuery(id+"F0.wireOp",EDGE,"E18");var subQ1=sQuery(id+"F0.wireOp",EDGE,"E17");Q3=makeQuery(id+"F7.boolean.opBoolean","MERGE",FACE,{"derivedFrom":[makeQuery(id+"F2.opRevolve","SWEPT_FACE",FACE,{"disambiguationData":[OSD([sQuery(id+"F0.wireOp",EDGE,"E16")])]}),makeQuery(id+"F7.opExtrude","CAP_FACE",FACE,{"disambiguationData":[OSD([subQ1,subQ0,sQuery(id+"F6.wireOp",EDGE,"E23.0.1"),sQuery(id+"F6.wireOp",EDGE,"E25")])],"isStart":false}),makeQuery(id+"F7.opExtrude","CAP_FACE",FACE,{"disambiguationData":[OSD([subQ1,subQ0,sQuery(id+"F6.wireOp",EDGE,"E23.0.3"),sQuery(id+"F6.wireOp",EDGE,"E24")])],"isStart":false}),makeQuery(id+"F7.opExtrude","CAP_FACE",FACE,{"disambiguationData":[OSD([subQ1,subQ0,sQuery(id+"F6.wireOp",EDGE,"E23.0.5"),sQuery(id+"F6.wireOp",EDGE,"E26")])],"isStart":false})]});}
            extrude(context, id + "F13", {"entities" : qUnion([Q0, Q1, Q2]), "operationType" : NewBodyOperationType.ADD, "endBound" : BoundingType.UP_TO_SURFACE, "oppositeDirection" : true, "endBoundEntityFace" : qUnion([Q3]), "depth" : 25 * mm});
        }
        {
            var Q0;
            Q0=makeQuery(id+"F12.imprint","IMPRINT",FACE,{"disambiguationData":[TD([[makeQuery(id+"F12.imprint","IMPRINT",EDGE,{"derivedFrom":sQuery(id+"F12.wireOp",EDGE,"E29.0")}),-1.0]])]});
            extrude(context, id + "F14", {"entities" : qUnion([Q0]), "operationType" : NewBodyOperationType.REMOVE, "oppositeDirection" : true, "depth" : 2.5 * mm});
        }
        {
            var Q0;
            {var subQ0=sQuery(id+"F12.wireOp",EDGE,"E31.2.5");var subQ1=sQuery(id+"F12.wireOp",EDGE,"E31.2.4");var subQ2=makeQuery(id+"F12.imprint","INTERSECT",VERTEX,{"derivedFrom":[subQ1,subQ0]});Q0=makeQuery(id+"F12.imprint","IMPRINT",FACE,{"disambiguationData":[TD([[makeQuery(id+"F12.imprint","IMPRINT",EDGE,{"disambiguationData":[TD([[subQ2,-1.0]])],"derivedFrom":subQ1}),-1.0]])]});}
            var Q1;
            {var subQ0=sQuery(id+"F12.wireOp",EDGE,"E31.2.4");var subQ1=sQuery(id+"F12.wireOp",EDGE,"E31.2.0");var subQ2=makeQuery(id+"F12.imprint","INTERSECT",VERTEX,{"derivedFrom":[subQ1,subQ0]});Q1=makeQuery(id+"F12.imprint","IMPRINT",FACE,{"disambiguationData":[TD([[makeQuery(id+"F12.imprint","IMPRINT",EDGE,{"disambiguationData":[TD([[subQ2,-1.0]])],"derivedFrom":subQ1}),-1.0]])]});}
            var Q2;
            {var subQ0=sQuery(id+"F12.wireOp",EDGE,"E31.2.1");var subQ1=sQuery(id+"F12.wireOp",EDGE,"E31.2.0");var subQ2=makeQuery(id+"F12.imprint","INTERSECT",VERTEX,{"derivedFrom":[subQ1,subQ0]});Q2=makeQuery(id+"F12.imprint","IMPRINT",FACE,{"disambiguationData":[TD([[makeQuery(id+"F12.imprint","IMPRINT",EDGE,{"disambiguationData":[TD([[subQ2,1.0]])],"derivedFrom":subQ1}),-1.0]])]});}
            var Q3;
            {var subQ0=sQuery(id+"F12.wireOp",EDGE,"E31.1.5");var subQ1=sQuery(id+"F12.wireOp",EDGE,"E31.1.4");var subQ2=makeQuery(id+"F12.imprint","INTERSECT",VERTEX,{"derivedFrom":[subQ1,subQ0]});Q3=makeQuery(id+"F12.imprint","IMPRINT",FACE,{"disambiguationData":[TD([[makeQuery(id+"F12.imprint","IMPRINT",EDGE,{"disambiguationData":[TD([[subQ2,-1.0]])],"derivedFrom":subQ1}),-1.0]])]});}
            var Q4;
            {var subQ0=sQuery(id+"F12.wireOp",EDGE,"E31.1.4");var subQ1=sQuery(id+"F12.wireOp",EDGE,"E31.1.0");var subQ2=makeQuery(id+"F12.imprint","INTERSECT",VERTEX,{"derivedFrom":[subQ1,subQ0]});Q4=makeQuery(id+"F12.imprint","IMPRINT",FACE,{"disambiguationData":[TD([[makeQuery(id+"F12.imprint","IMPRINT",EDGE,{"disambiguationData":[TD([[subQ2,-1.0]])],"derivedFrom":subQ1}),-1.0]])]});}
            var Q5;
            {var subQ0=sQuery(id+"F12.wireOp",EDGE,"E31.1.1");var subQ1=sQuery(id+"F12.wireOp",EDGE,"E31.1.0");var subQ2=makeQuery(id+"F12.imprint","INTERSECT",VERTEX,{"derivedFrom":[subQ1,subQ0]});Q5=makeQuery(id+"F12.imprint","IMPRINT",FACE,{"disambiguationData":[TD([[makeQuery(id+"F12.imprint","IMPRINT",EDGE,{"disambiguationData":[TD([[subQ2,1.0]])],"derivedFrom":subQ1}),-1.0]])]});}
            var Q6;
            {var subQ0=sQuery(id+"F12.wireOp",EDGE,"E30.4");var subQ1=sQuery(id+"F6.wireOp",EDGE,"E23.0.3");var subQ2=sQuery(id+"F12.wireOp",EDGE,"E30.3");var subQ3=sQuery(id+"F0.wireOp",EDGE,"E18");var subQ4=sQuery(id+"F0.wireOp",EDGE,"E17");Q6=makeQuery(id+"F13.boolean.opBoolean","MERGE",FACE,{"derivedFrom":[makeQuery(id+"F7.boolean.opBoolean","MERGE",FACE,{"derivedFrom":[makeQuery(id+"F2.opRevolve","SWEPT_FACE",FACE,{"disambiguationData":[OSD([sQuery(id+"F0.wireOp",EDGE,"E16")])]}),makeQuery(id+"F7.opExtrude","CAP_FACE",FACE,{"disambiguationData":[OSD([subQ4,subQ3,sQuery(id+"F6.wireOp",EDGE,"E23.0.1"),sQuery(id+"F6.wireOp",EDGE,"E25")])],"isStart":false}),makeQuery(id+"F7.opExtrude","CAP_FACE",FACE,{"disambiguationData":[OSD([subQ4,subQ3,subQ1,sQuery(id+"F6.wireOp",EDGE,"E24")])],"isStart":false}),makeQuery(id+"F7.opExtrude","CAP_FACE",FACE,{"disambiguationData":[OSD([subQ4,subQ3,sQuery(id+"F6.wireOp",EDGE,"E23.0.5"),sQuery(id+"F6.wireOp",EDGE,"E26")])],"isStart":false})]}),makeQuery(id+"F13.opExtrude","CAP_FACE",FACE,{"disambiguationData":[OSD([subQ1,sQuery(id+"F12.wireOp",EDGE,"E30.2"),subQ2])],"isStart":false}),makeQuery(id+"F13.opExtrude","CAP_FACE",FACE,{"disambiguationData":[OSD([subQ1,subQ2,subQ0])],"isStart":false}),makeQuery(id+"F13.opExtrude","CAP_FACE",FACE,{"disambiguationData":[OSD([subQ1,subQ0,sQuery(id+"F12.wireOp",EDGE,"E30.5")])],"isStart":false})]});}
            extrude(context, id + "F15", {"entities" : qUnion([Q0, Q1, Q2, Q3, Q4, Q5]), "operationType" : NewBodyOperationType.ADD, "endBound" : BoundingType.UP_TO_SURFACE, "oppositeDirection" : true, "endBoundEntityFace" : qUnion([Q6]), "depth" : 25 * mm});
        }
        {
            var Q0;
            Q0=makeQuery(id+"F12.imprint","IMPRINT",FACE,{"disambiguationData":[TD([[makeQuery(id+"F12.imprint","IMPRINT",EDGE,{"derivedFrom":sQuery(id+"F12.wireOp",EDGE,"E31.1.2")}),-1.0]])]});
            var Q1;
            Q1=makeQuery(id+"F12.imprint","IMPRINT",FACE,{"disambiguationData":[TD([[makeQuery(id+"F12.imprint","IMPRINT",EDGE,{"derivedFrom":sQuery(id+"F12.wireOp",EDGE,"E31.2.2")}),-1.0]])]});
            extrude(context, id + "F16", {"entities" : qUnion([Q0, Q1]), "operationType" : NewBodyOperationType.REMOVE, "oppositeDirection" : true, "depth" : 2.5 * mm});
        }
        {
            var Q0;
            {var subQ0=sQuery(id+"F12.wireOp",EDGE,"E31.2.4");var subQ1=sQuery(id+"F6.wireOp",EDGE,"E23.0.1");var subQ2=sQuery(id+"F12.wireOp",EDGE,"E31.2.0");var subQ3=sQuery(id+"F12.wireOp",EDGE,"E31.1.4");var subQ4=sQuery(id+"F6.wireOp",EDGE,"E23.0.5");var subQ5=sQuery(id+"F12.wireOp",EDGE,"E31.1.0");var subQ6=sQuery(id+"F12.wireOp",EDGE,"E30.4");var subQ7=sQuery(id+"F6.wireOp",EDGE,"E23.0.3");var subQ8=sQuery(id+"F12.wireOp",EDGE,"E30.3");var subQ9=sQuery(id+"F0.wireOp",EDGE,"E18");var subQ10=sQuery(id+"F0.wireOp",EDGE,"E17");Q0=makeQuery(id+"F15.boolean.opBoolean","MERGE",FACE,{"derivedFrom":[makeQuery(id+"F13.boolean.opBoolean","MERGE",FACE,{"derivedFrom":[makeQuery(id+"F7.boolean.opBoolean","MERGE",FACE,{"derivedFrom":[makeQuery(id+"F2.opRevolve","SWEPT_FACE",FACE,{"disambiguationData":[OSD([subQ9])]}),makeQuery(id+"F7.opExtrude","CAP_FACE",FACE,{"disambiguationData":[OSD([subQ10,subQ9,subQ1,sQuery(id+"F6.wireOp",EDGE,"E25")])],"isStart":true}),makeQuery(id+"F7.opExtrude","CAP_FACE",FACE,{"disambiguationData":[OSD([subQ10,subQ9,subQ7,sQuery(id+"F6.wireOp",EDGE,"E24")])],"isStart":true}),makeQuery(id+"F7.opExtrude","CAP_FACE",FACE,{"disambiguationData":[OSD([subQ10,subQ9,subQ4,sQuery(id+"F6.wireOp",EDGE,"E26")])],"isStart":true})]}),makeQuery(id+"F13.opExtrude","CAP_FACE",FACE,{"disambiguationData":[OSD([subQ7,sQuery(id+"F12.wireOp",EDGE,"E30.2"),subQ8])],"isStart":true}),makeQuery(id+"F13.opExtrude","CAP_FACE",FACE,{"disambiguationData":[OSD([subQ7,subQ8,subQ6])],"isStart":true}),makeQuery(id+"F13.opExtrude","CAP_FACE",FACE,{"disambiguationData":[OSD([subQ7,subQ6,sQuery(id+"F12.wireOp",EDGE,"E30.5")])],"isStart":true})]}),makeQuery(id+"F15.opExtrude","CAP_FACE",FACE,{"disambiguationData":[OSD([subQ4,subQ5,subQ3])],"isStart":true}),makeQuery(id+"F15.opExtrude","CAP_FACE",FACE,{"disambiguationData":[OSD([subQ4,subQ5,sQuery(id+"F12.wireOp",EDGE,"E31.1.1")])],"isStart":true}),makeQuery(id+"F15.opExtrude","CAP_FACE",FACE,{"disambiguationData":[OSD([subQ4,subQ3,sQuery(id+"F12.wireOp",EDGE,"E31.1.5")])],"isStart":true}),makeQuery(id+"F15.opExtrude","CAP_FACE",FACE,{"disambiguationData":[OSD([subQ1,subQ2,subQ0])],"isStart":true}),makeQuery(id+"F15.opExtrude","CAP_FACE",FACE,{"disambiguationData":[OSD([subQ1,subQ2,sQuery(id+"F12.wireOp",EDGE,"E31.2.1")])],"isStart":true}),makeQuery(id+"F15.opExtrude","CAP_FACE",FACE,{"disambiguationData":[OSD([subQ1,subQ0,sQuery(id+"F12.wireOp",EDGE,"E31.2.5")])],"isStart":true})]});}
            chamfer(context, id + "F17", {"entities" : qUnion([Q0]), "width" : .25 * mm, "tangentPropagation" : true});
        }
        {
            var Q0;
            {var subQ0=sQuery(id+"F0.wireOp",EDGE,"E13");var subQ1=sQuery(id+"F0.wireOp",EDGE,"E12");Q0=makeQuery(id+"F4.boolean.opBoolean","MERGE",FACE,{"derivedFrom":[makeQuery(id+"F2.opRevolve","SWEPT_FACE",FACE,{"disambiguationData":[OSD([sQuery(id+"F0.wireOp",EDGE,"E14")])]}),makeQuery(id+"F4.opExtrude","CAP_FACE",FACE,{"disambiguationData":[OSD([subQ1,subQ0,sQuery(id+"F3.wireOp",EDGE,"E20"),sQuery(id+"F3.wireOp",EDGE,"E21")])],"isStart":false}),makeQuery(id+"F4.opExtrude","CAP_FACE",FACE,{"disambiguationData":[OSD([subQ1,subQ0,sQuery(id+"F3.wireOp",EDGE,"E22.1.0"),sQuery(id+"F3.wireOp",EDGE,"E22.1.1")])],"isStart":false}),makeQuery(id+"F4.opExtrude","CAP_FACE",FACE,{"disambiguationData":[OSD([subQ1,subQ0,sQuery(id+"F3.wireOp",EDGE,"E22.2.0"),sQuery(id+"F3.wireOp",EDGE,"E22.2.1")])],"isStart":false})]});}
            var Q1;
            {var subQ0=sQuery(id+"F12.wireOp",EDGE,"E31.2.4");var subQ1=sQuery(id+"F6.wireOp",EDGE,"E23.0.1");var subQ2=sQuery(id+"F12.wireOp",EDGE,"E31.2.0");var subQ3=sQuery(id+"F12.wireOp",EDGE,"E31.1.4");var subQ4=sQuery(id+"F6.wireOp",EDGE,"E23.0.5");var subQ5=sQuery(id+"F12.wireOp",EDGE,"E31.1.0");var subQ6=sQuery(id+"F12.wireOp",EDGE,"E30.4");var subQ7=sQuery(id+"F6.wireOp",EDGE,"E23.0.3");var subQ8=sQuery(id+"F12.wireOp",EDGE,"E30.3");var subQ9=sQuery(id+"F0.wireOp",EDGE,"E18");var subQ10=sQuery(id+"F0.wireOp",EDGE,"E17");Q1=makeQuery(id+"F15.boolean.opBoolean","MERGE",FACE,{"derivedFrom":[makeQuery(id+"F13.boolean.opBoolean","MERGE",FACE,{"derivedFrom":[makeQuery(id+"F7.boolean.opBoolean","MERGE",FACE,{"derivedFrom":[makeQuery(id+"F2.opRevolve","SWEPT_FACE",FACE,{"disambiguationData":[OSD([sQuery(id+"F0.wireOp",EDGE,"E16")])]}),makeQuery(id+"F7.opExtrude","CAP_FACE",FACE,{"disambiguationData":[OSD([subQ10,subQ9,subQ1,sQuery(id+"F6.wireOp",EDGE,"E25")])],"isStart":false}),makeQuery(id+"F7.opExtrude","CAP_FACE",FACE,{"disambiguationData":[OSD([subQ10,subQ9,subQ7,sQuery(id+"F6.wireOp",EDGE,"E24")])],"isStart":false}),makeQuery(id+"F7.opExtrude","CAP_FACE",FACE,{"disambiguationData":[OSD([subQ10,subQ9,subQ4,sQuery(id+"F6.wireOp",EDGE,"E26")])],"isStart":false})]}),makeQuery(id+"F13.opExtrude","CAP_FACE",FACE,{"disambiguationData":[OSD([subQ7,sQuery(id+"F12.wireOp",EDGE,"E30.2"),subQ8])],"isStart":false}),makeQuery(id+"F13.opExtrude","CAP_FACE",FACE,{"disambiguationData":[OSD([subQ7,subQ8,subQ6])],"isStart":false}),makeQuery(id+"F13.opExtrude","CAP_FACE",FACE,{"disambiguationData":[OSD([subQ7,subQ6,sQuery(id+"F12.wireOp",EDGE,"E30.5")])],"isStart":false})]}),makeQuery(id+"F15.opExtrude","CAP_FACE",FACE,{"disambiguationData":[OSD([subQ4,subQ5,subQ3])],"isStart":false}),makeQuery(id+"F15.opExtrude","CAP_FACE",FACE,{"disambiguationData":[OSD([subQ4,subQ5,sQuery(id+"F12.wireOp",EDGE,"E31.1.1")])],"isStart":false}),makeQuery(id+"F15.opExtrude","CAP_FACE",FACE,{"disambiguationData":[OSD([subQ4,subQ3,sQuery(id+"F12.wireOp",EDGE,"E31.1.5")])],"isStart":false}),makeQuery(id+"F15.opExtrude","CAP_FACE",FACE,{"disambiguationData":[OSD([subQ1,subQ2,subQ0])],"isStart":false}),makeQuery(id+"F15.opExtrude","CAP_FACE",FACE,{"disambiguationData":[OSD([subQ1,subQ2,sQuery(id+"F12.wireOp",EDGE,"E31.2.1")])],"isStart":false}),makeQuery(id+"F15.opExtrude","CAP_FACE",FACE,{"disambiguationData":[OSD([subQ1,subQ0,sQuery(id+"F12.wireOp",EDGE,"E31.2.5")])],"isStart":false})]});}
            var Q2;
            {var subQ0=sQuery(id+"F0.wireOp",EDGE,"E13");var subQ1=sQuery(id+"F0.wireOp",EDGE,"E12");Q2=makeQuery(id+"F4.boolean.opBoolean","MERGE",FACE,{"derivedFrom":[makeQuery(id+"F2.opRevolve","SWEPT_FACE",FACE,{"disambiguationData":[OSD([subQ1])]}),makeQuery(id+"F4.opExtrude","CAP_FACE",FACE,{"disambiguationData":[OSD([subQ1,subQ0,sQuery(id+"F3.wireOp",EDGE,"E20"),sQuery(id+"F3.wireOp",EDGE,"E21")])],"isStart":true}),makeQuery(id+"F4.opExtrude","CAP_FACE",FACE,{"disambiguationData":[OSD([subQ1,subQ0,sQuery(id+"F3.wireOp",EDGE,"E22.1.0"),sQuery(id+"F3.wireOp",EDGE,"E22.1.1")])],"isStart":true}),makeQuery(id+"F4.opExtrude","CAP_FACE",FACE,{"disambiguationData":[OSD([subQ1,subQ0,sQuery(id+"F3.wireOp",EDGE,"E22.2.0"),sQuery(id+"F3.wireOp",EDGE,"E22.2.1")])],"isStart":true})]});}
            chamfer(context, id + "F18", {"entities" : qUnion([Q0, Q1, Q2]), "width" : .5 * mm, "tangentPropagation" : true});
        }
        {
            var Q0;
            Q0=makeQuery(id+"F14.boolean.opBoolean","COPY",FACE,{"derivedFrom":makeQuery(id+"F14.opExtrude","CAP_FACE",FACE,{"disambiguationData":[OSD([sQuery(id+"F6.wireOp",EDGE,"E24"),sQuery(id+"F12.wireOp",EDGE,"E29.0"),sQuery(id+"F12.wireOp",EDGE,"E29.1"),sQuery(id+"F12.wireOp",EDGE,"E29.2"),sQuery(id+"F12.wireOp",EDGE,"E29.3"),sQuery(id+"F12.wireOp",EDGE,"E29.4"),sQuery(id+"F12.wireOp",EDGE,"E29.5")])],"isStart":false})});
            var sketch = newSketch(context, id + "F19", { "sketchPlane" : qUnion([Q0])});
            skCircle(sketch, "E32.0", {"center": v(-8.66, -9.65) * mm, "radius": 1.75 * mm});
            skCircle(sketch, "E33.0", {"center": v(8.66, -9.65) * mm, "radius": 1.75 * mm});
            skCircle(sketch, "E34.0", {"center": v(0, 5.35) * mm, "radius": 1.75 * mm});
            skCircle(sketch, "E35", {"center": v(-8.66, -9.65) * mm, "radius": 2.5 * mm});
            skCircle(sketch, "E36", {"center": v(0, 5.35) * mm, "radius": 2.5 * mm});
            skCircle(sketch, "E37", {"center": v(8.66, -9.65) * mm, "radius": 2.5 * mm});
            skSolve(sketch);
        }
        {
            var Q0;
            Q0=makeQuery(id+"F19.imprint","IMPRINT",FACE,{"disambiguationData":[TD([[makeQuery(id+"F19.imprint","IMPRINT",EDGE,{"derivedFrom":sQuery(id+"F19.wireOp",EDGE,"E32.0")}),-1.0]])]});
            var Q1;
            Q1=makeQuery(id+"F19.imprint","IMPRINT",FACE,{"disambiguationData":[TD([[makeQuery(id+"F19.imprint","IMPRINT",EDGE,{"derivedFrom":sQuery(id+"F19.wireOp",EDGE,"E34.0")}),-1.0]])]});
            var Q2;
            Q2=makeQuery(id+"F19.imprint","IMPRINT",FACE,{"disambiguationData":[TD([[makeQuery(id+"F19.imprint","IMPRINT",EDGE,{"derivedFrom":sQuery(id+"F19.wireOp",EDGE,"E33.0")}),-1.0]])]});
            extrude(context, id + "F20", {"entities" : qUnion([Q0, Q1, Q2]), "operationType" : NewBodyOperationType.REMOVE, "oppositeDirection" : true, "depth" : 5 * mm, "offsetDistance" : 25 * mm});
        }
    });
